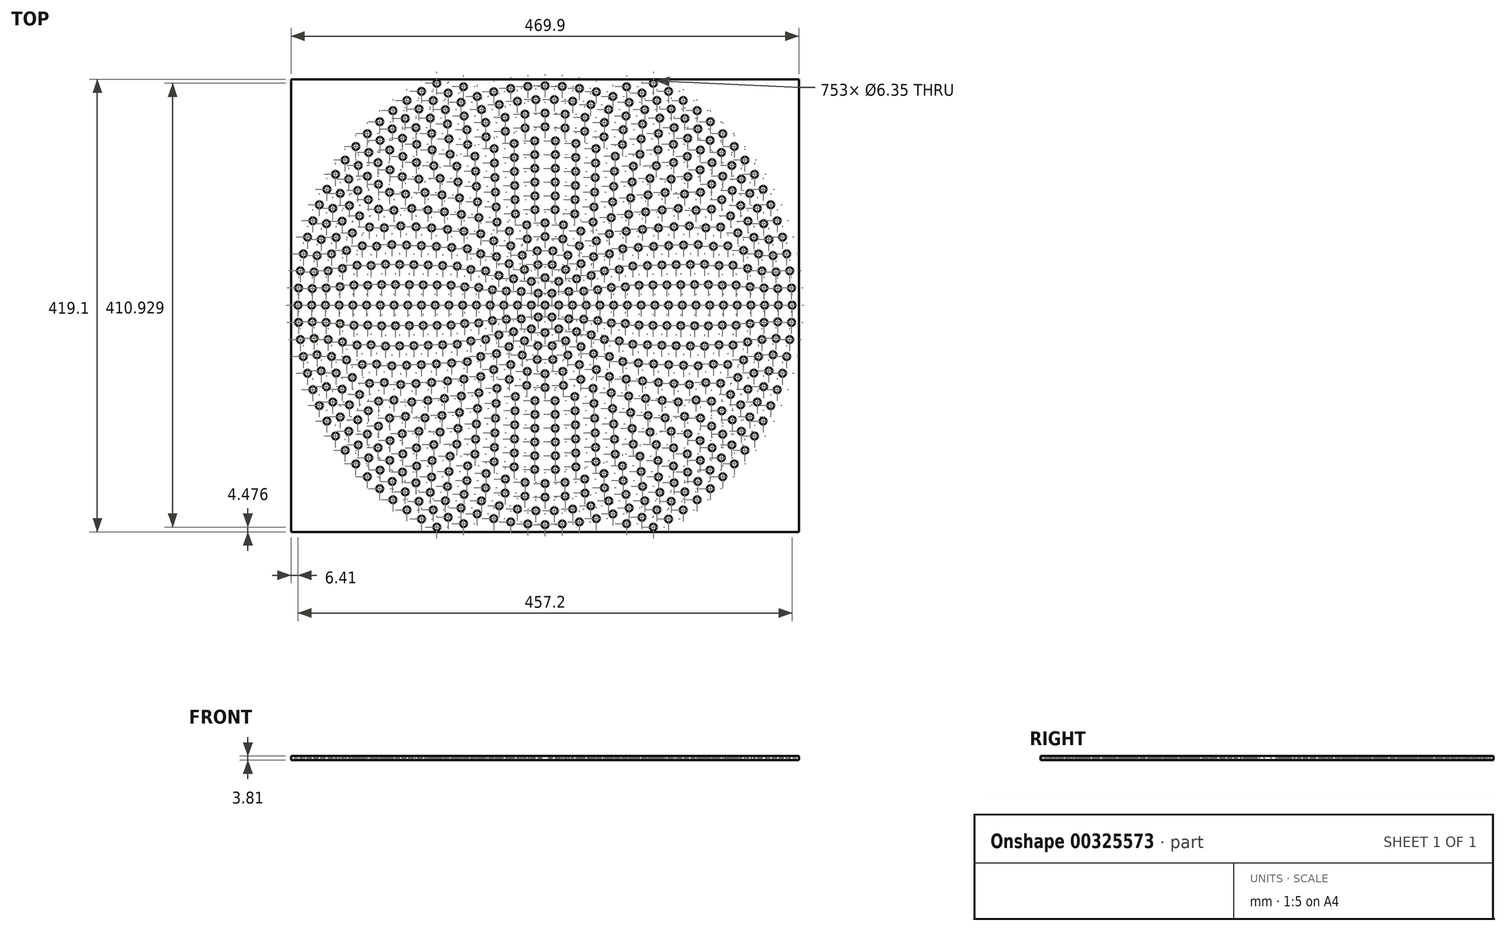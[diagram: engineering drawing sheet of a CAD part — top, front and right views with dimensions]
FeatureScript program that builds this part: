
annotation { "Feature Type Name" : "Feature", "Feature Type Description" : "" }
export const myFeature = defineFeature(function(context is Context, id is Id, definition is map)
    precondition{}
    {
        {
            var Q0;
            Q0=qCreatedBy(makeId("Top.planeOp"),FACE);
            var sketch = newSketch(context, id + "F0", { "sketchPlane" : qUnion([Q0])});
            skLineSegment(sketch, "E0.bottom", {"start": v(-235, 209.16) * mm, "end": v(234.9, 209.16) * mm});
            skLineSegment(sketch, "E0.top", {"start": v(-235, -209.94) * mm, "end": v(234.9, -209.94) * mm});
            skLineSegment(sketch, "E0.left", {"start": v(-235, 209.16) * mm, "end": v(-235, -209.94) * mm});
            skLineSegment(sketch, "E0.right", {"start": v(234.9, 209.16) * mm, "end": v(234.9, -209.94) * mm});
            skPoint(sketch, "E1", {"position": v(-0.06, -209.94) * mm});
            skPoint(sketch, "E2", {"position": v(234.9, -0.39) * mm});
            skCircle(sketch, "E3", {"center": v(0, 0) * mm, "radius": 3.18 * mm});
            skCircle(sketch, "E4.1.0.0", {"center": v(12.7, 0) * mm, "radius": 3.18 * mm});
            skCircle(sketch, "E4.2.0.0", {"center": v(25.4, 0) * mm, "radius": 3.18 * mm});
            skCircle(sketch, "E4.3.0.0", {"center": v(38.1, 0) * mm, "radius": 3.18 * mm});
            skCircle(sketch, "E4.4.0.0", {"center": v(50.8, 0) * mm, "radius": 3.18 * mm});
            skCircle(sketch, "E4.5.0.0", {"center": v(63.5, 0) * mm, "radius": 3.18 * mm});
            skCircle(sketch, "E4.6.0.0", {"center": v(76.2, 0) * mm, "radius": 3.18 * mm});
            skCircle(sketch, "E4.7.0.0", {"center": v(88.9, 0) * mm, "radius": 3.18 * mm});
            skCircle(sketch, "E4.8.0.0", {"center": v(101.6, 0) * mm, "radius": 3.18 * mm});
            skCircle(sketch, "E4.9.0.0", {"center": v(114.3, 0) * mm, "radius": 3.18 * mm});
            skCircle(sketch, "E4.10.0.0", {"center": v(127, 0) * mm, "radius": 3.18 * mm});
            skCircle(sketch, "E4.11.0.0", {"center": v(139.7, 0) * mm, "radius": 3.18 * mm});
            skCircle(sketch, "E4.12.0.0", {"center": v(152.4, 0) * mm, "radius": 3.18 * mm});
            skCircle(sketch, "E4.13.0.0", {"center": v(165.1, 0) * mm, "radius": 3.18 * mm});
            skCircle(sketch, "E4.14.0.0", {"center": v(177.8, 0) * mm, "radius": 3.18 * mm});
            skCircle(sketch, "E4.15.0.0", {"center": v(190.5, 0) * mm, "radius": 3.18 * mm});
            skCircle(sketch, "E4.16.0.0", {"center": v(203.2, 0) * mm, "radius": 3.18 * mm});
            skCircle(sketch, "E4.17.0.0", {"center": v(215.9, 0) * mm, "radius": 3.18 * mm});
            skCircle(sketch, "E4.18.0.0", {"center": v(228.6, 0) * mm, "radius": 3.18 * mm});
            skLineSegment(sketch, "E4.direction1", {"start": v(0, 0) * mm, "end": v(12.7, 0) * mm, "construction": true});
            skCircle(sketch, "E5.1.0", {"center": v(6.35, 11) * mm, "radius": 3.18 * mm});
            skCircle(sketch, "E5.2.0", {"center": v(-6.35, 11) * mm, "radius": 3.18 * mm});
            skCircle(sketch, "E5.3.0", {"center": v(-12.7, 0) * mm, "radius": 3.18 * mm});
            skCircle(sketch, "E5.4.0", {"center": v(-6.35, -11) * mm, "radius": 3.18 * mm});
            skCircle(sketch, "E5.5.0", {"center": v(6.35, -11) * mm, "radius": 3.18 * mm});
            skCircle(sketch, "E6.1.0", {"center": v(22, -12.7) * mm, "radius": 3.18 * mm});
            skCircle(sketch, "E6.2.0", {"center": v(12.7, -22) * mm, "radius": 3.18 * mm});
            skCircle(sketch, "E6.3.0", {"center": v(0, -25.4) * mm, "radius": 3.18 * mm});
            skCircle(sketch, "E6.4.0", {"center": v(-12.7, -22) * mm, "radius": 3.18 * mm});
            skCircle(sketch, "E6.5.0", {"center": v(-22, -12.7) * mm, "radius": 3.18 * mm});
            skCircle(sketch, "E6.6.0", {"center": v(-25.4, 0) * mm, "radius": 3.18 * mm});
            skLineSegment(sketch, "E6.anchor1", {"start": v(0, 0) * mm, "end": v(25.4, 0) * mm, "construction": true});
            skLineSegment(sketch, "E6.anchor2", {"start": v(0, 0) * mm, "end": v(-25.4, 0) * mm, "construction": true});
            skCircle(sketch, "E7.1.0", {"center": v(-22, 12.7) * mm, "radius": 3.18 * mm});
            skCircle(sketch, "E7.2.0", {"center": v(-12.7, 22) * mm, "radius": 3.18 * mm});
            skCircle(sketch, "E7.3.0", {"center": v(0, 25.4) * mm, "radius": 3.18 * mm});
            skCircle(sketch, "E7.4.0", {"center": v(12.7, 22) * mm, "radius": 3.18 * mm});
            skCircle(sketch, "E7.5.0", {"center": v(22, 12.7) * mm, "radius": 3.18 * mm});
            skCircle(sketch, "E8.1.0", {"center": v(35.8, 13.03) * mm, "radius": 3.18 * mm});
            skCircle(sketch, "E8.2.0", {"center": v(29.19, 24.5) * mm, "radius": 3.17 * mm});
            skCircle(sketch, "E8.3.0", {"center": v(19.05, 33) * mm, "radius": 3.18 * mm});
            skCircle(sketch, "E8.4.0", {"center": v(6.62, 37.52) * mm, "radius": 3.17 * mm});
            skCircle(sketch, "E8.5.0", {"center": v(-6.62, 37.52) * mm, "radius": 3.17 * mm});
            skCircle(sketch, "E8.6.0", {"center": v(-19.05, 33) * mm, "radius": 3.17 * mm});
            skCircle(sketch, "E8.7.0", {"center": v(-29.19, 24.5) * mm, "radius": 3.18 * mm});
            skCircle(sketch, "E8.8.0", {"center": v(-35.8, 13.03) * mm, "radius": 3.17 * mm});
            skCircle(sketch, "E8.9.0", {"center": v(-38.1, 0) * mm, "radius": 3.18 * mm});
            skCircle(sketch, "E8.10.0", {"center": v(-35.8, -13.03) * mm, "radius": 3.18 * mm});
            skCircle(sketch, "E9.1.11.0", {"center": v(-29.19, -24.5) * mm, "radius": 3.18 * mm});
            skCircle(sketch, "E10.1.12.0", {"center": v(-19.05, -33) * mm, "radius": 3.18 * mm});
            skCircle(sketch, "E11.1.13.0", {"center": v(-6.62, -37.52) * mm, "radius": 3.18 * mm});
            skCircle(sketch, "E11.1.14.0", {"center": v(6.62, -37.52) * mm, "radius": 3.18 * mm});
            skCircle(sketch, "E12.1.15.0", {"center": v(19.05, -33) * mm, "radius": 3.18 * mm});
            skCircle(sketch, "E13.1.16.0", {"center": v(29.19, -24.5) * mm, "radius": 3.18 * mm});
            skCircle(sketch, "E13.1.17.0", {"center": v(35.8, -13.03) * mm, "radius": 3.18 * mm});
            skCircle(sketch, "E14.1.0", {"center": v(48.74, 14.31) * mm, "radius": 3.17 * mm});
            skCircle(sketch, "E14.2.0", {"center": v(42.74, 27.46) * mm, "radius": 3.18 * mm});
            skCircle(sketch, "E14.3.0", {"center": v(33.27, 38.4) * mm, "radius": 3.18 * mm});
            skCircle(sketch, "E14.4.0", {"center": v(21.1, 46.2) * mm, "radius": 3.17 * mm});
            skCircle(sketch, "E14.5.0", {"center": v(7.23, 50.28) * mm, "radius": 3.18 * mm});
            skCircle(sketch, "E14.6.0", {"center": v(-7.23, 50.28) * mm, "radius": 3.18 * mm});
            skCircle(sketch, "E14.7.0", {"center": v(-21.1, 46.2) * mm, "radius": 3.17 * mm});
            skCircle(sketch, "E14.8.0", {"center": v(-33.27, 38.4) * mm, "radius": 3.17 * mm});
            skCircle(sketch, "E14.9.0", {"center": v(-42.74, 27.46) * mm, "radius": 3.17 * mm});
            skCircle(sketch, "E14.10.0", {"center": v(-48.74, 14.31) * mm, "radius": 3.17 * mm});
            skCircle(sketch, "E14.11.0", {"center": v(-50.8, 0) * mm, "radius": 3.17 * mm});
            skCircle(sketch, "E14.12.0", {"center": v(-48.74, -14.31) * mm, "radius": 3.18 * mm});
            skCircle(sketch, "E14.13.0", {"center": v(-42.74, -27.46) * mm, "radius": 3.18 * mm});
            skCircle(sketch, "E14.14.0", {"center": v(-33.27, -38.4) * mm, "radius": 3.18 * mm});
            skCircle(sketch, "E14.15.0", {"center": v(-21.1, -46.2) * mm, "radius": 3.18 * mm});
            skCircle(sketch, "E14.16.0", {"center": v(-7.23, -50.28) * mm, "radius": 3.18 * mm});
            skCircle(sketch, "E14.17.0", {"center": v(7.23, -50.28) * mm, "radius": 3.18 * mm});
            skCircle(sketch, "E14.18.0", {"center": v(21.1, -46.2) * mm, "radius": 3.18 * mm});
            skCircle(sketch, "E15.1.19.0", {"center": v(33.27, -38.4) * mm, "radius": 3.18 * mm});
            skCircle(sketch, "E16.1.20.0", {"center": v(42.74, -27.46) * mm, "radius": 3.18 * mm});
            skCircle(sketch, "E16.1.21.0", {"center": v(48.74, -14.31) * mm, "radius": 3.18 * mm});
            skCircle(sketch, "E17.1.0", {"center": v(61.34, 16.44) * mm, "radius": 3.18 * mm});
            skCircle(sketch, "E17.2.0", {"center": v(55, 31.75) * mm, "radius": 3.18 * mm});
            skCircle(sketch, "E17.3.0", {"center": v(44.9, 44.9) * mm, "radius": 3.18 * mm});
            skCircle(sketch, "E17.4.0", {"center": v(31.75, 55) * mm, "radius": 3.18 * mm});
            skCircle(sketch, "E17.5.0", {"center": v(16.44, 61.34) * mm, "radius": 3.18 * mm});
            skCircle(sketch, "E17.6.0", {"center": v(0, 63.5) * mm, "radius": 3.18 * mm});
            skCircle(sketch, "E17.7.0", {"center": v(-16.44, 61.34) * mm, "radius": 3.18 * mm});
            skCircle(sketch, "E17.8.0", {"center": v(-31.75, 55) * mm, "radius": 3.18 * mm});
            skCircle(sketch, "E17.9.0", {"center": v(-44.9, 44.9) * mm, "radius": 3.18 * mm});
            skCircle(sketch, "E17.10.0", {"center": v(-55, 31.75) * mm, "radius": 3.18 * mm});
            skCircle(sketch, "E17.11.0", {"center": v(-61.34, 16.44) * mm, "radius": 3.18 * mm});
            skCircle(sketch, "E17.12.0", {"center": v(-63.5, 0) * mm, "radius": 3.18 * mm});
            skCircle(sketch, "E17.13.0", {"center": v(-61.34, -16.44) * mm, "radius": 3.18 * mm});
            skCircle(sketch, "E17.14.0", {"center": v(-55, -31.75) * mm, "radius": 3.18 * mm});
            skCircle(sketch, "E17.15.0", {"center": v(-44.9, -44.9) * mm, "radius": 3.18 * mm});
            skCircle(sketch, "E17.16.0", {"center": v(-31.75, -55) * mm, "radius": 3.18 * mm});
            skCircle(sketch, "E17.17.0", {"center": v(-16.44, -61.34) * mm, "radius": 3.18 * mm});
            skCircle(sketch, "E17.18.0", {"center": v(0, -63.5) * mm, "radius": 3.18 * mm});
            skCircle(sketch, "E17.19.0", {"center": v(16.44, -61.34) * mm, "radius": 3.18 * mm});
            skCircle(sketch, "E17.20.0", {"center": v(31.75, -55) * mm, "radius": 3.18 * mm});
            skCircle(sketch, "E17.21.0", {"center": v(44.9, -44.9) * mm, "radius": 3.18 * mm});
            skCircle(sketch, "E17.22.0", {"center": v(55, -31.75) * mm, "radius": 3.18 * mm});
            skCircle(sketch, "E17.23.0", {"center": v(61.34, -16.44) * mm, "radius": 3.18 * mm});
            skCircle(sketch, "E18.1.0", {"center": v(74.29, 16.96) * mm, "radius": 3.18 * mm});
            skCircle(sketch, "E18.2.0", {"center": v(68.65, 33.06) * mm, "radius": 3.18 * mm});
            skCircle(sketch, "E18.3.0", {"center": v(59.58, 47.5) * mm, "radius": 3.18 * mm});
            skCircle(sketch, "E18.4.0", {"center": v(47.5, 59.58) * mm, "radius": 3.18 * mm});
            skCircle(sketch, "E18.5.0", {"center": v(33.06, 68.65) * mm, "radius": 3.18 * mm});
            skCircle(sketch, "E18.6.0", {"center": v(16.96, 74.29) * mm, "radius": 3.18 * mm});
            skCircle(sketch, "E18.7.0", {"center": v(0, 76.2) * mm, "radius": 3.18 * mm});
            skCircle(sketch, "E18.8.0", {"center": v(-16.96, 74.29) * mm, "radius": 3.18 * mm});
            skCircle(sketch, "E18.9.0", {"center": v(-33.06, 68.65) * mm, "radius": 3.18 * mm});
            skCircle(sketch, "E18.10.0", {"center": v(-47.5, 59.58) * mm, "radius": 3.18 * mm});
            skCircle(sketch, "E18.11.0", {"center": v(-59.58, 47.5) * mm, "radius": 3.17 * mm});
            skCircle(sketch, "E18.12.0", {"center": v(-68.65, 33.06) * mm, "radius": 3.17 * mm});
            skCircle(sketch, "E18.13.0", {"center": v(-74.29, 16.96) * mm, "radius": 3.18 * mm});
            skCircle(sketch, "E18.14.0", {"center": v(-76.2, 0) * mm, "radius": 3.18 * mm});
            skCircle(sketch, "E18.15.0", {"center": v(-74.29, -16.96) * mm, "radius": 3.18 * mm});
            skCircle(sketch, "E18.16.0", {"center": v(-68.65, -33.06) * mm, "radius": 3.17 * mm});
            skCircle(sketch, "E18.17.0", {"center": v(-59.58, -47.5) * mm, "radius": 3.18 * mm});
            skCircle(sketch, "E18.18.0", {"center": v(-47.5, -59.58) * mm, "radius": 3.18 * mm});
            skCircle(sketch, "E18.19.0", {"center": v(-33.06, -68.65) * mm, "radius": 3.18 * mm});
            skCircle(sketch, "E18.20.0", {"center": v(-16.96, -74.29) * mm, "radius": 3.18 * mm});
            skCircle(sketch, "E18.21.0", {"center": v(0, -76.2) * mm, "radius": 3.17 * mm});
            skCircle(sketch, "E18.22.0", {"center": v(16.96, -74.29) * mm, "radius": 3.18 * mm});
            skCircle(sketch, "E18.23.0", {"center": v(33.06, -68.65) * mm, "radius": 3.18 * mm});
            skCircle(sketch, "E18.24.0", {"center": v(47.5, -59.58) * mm, "radius": 3.18 * mm});
            skCircle(sketch, "E18.25.0", {"center": v(59.58, -47.5) * mm, "radius": 3.18 * mm});
            skCircle(sketch, "E19.1.0", {"center": v(86.96, 18.48) * mm, "radius": 3.18 * mm});
            skCircle(sketch, "E19.2.0", {"center": v(81.21, 36.16) * mm, "radius": 3.18 * mm});
            skCircle(sketch, "E19.3.0", {"center": v(71.92, 52.25) * mm, "radius": 3.18 * mm});
            skCircle(sketch, "E19.4.0", {"center": v(59.49, 66.07) * mm, "radius": 3.18 * mm});
            skCircle(sketch, "E19.5.0", {"center": v(44.45, 76.99) * mm, "radius": 3.18 * mm});
            skCircle(sketch, "E19.6.0", {"center": v(27.47, 84.55) * mm, "radius": 3.18 * mm});
            skCircle(sketch, "E19.7.0", {"center": v(9.3, 88.41) * mm, "radius": 3.18 * mm});
            skCircle(sketch, "E19.8.0", {"center": v(-9.3, 88.41) * mm, "radius": 3.18 * mm});
            skCircle(sketch, "E19.9.0", {"center": v(-27.47, 84.55) * mm, "radius": 3.18 * mm});
            skCircle(sketch, "E19.10.0", {"center": v(-44.45, 76.99) * mm, "radius": 3.18 * mm});
            skCircle(sketch, "E19.11.0", {"center": v(-59.49, 66.07) * mm, "radius": 3.17 * mm});
            skCircle(sketch, "E19.12.0", {"center": v(-71.92, 52.25) * mm, "radius": 3.18 * mm});
            skCircle(sketch, "E19.13.0", {"center": v(-81.21, 36.16) * mm, "radius": 3.18 * mm});
            skCircle(sketch, "E19.14.0", {"center": v(-86.96, 18.48) * mm, "radius": 3.18 * mm});
            skCircle(sketch, "E19.15.0", {"center": v(-88.9, 0) * mm, "radius": 3.18 * mm});
            skCircle(sketch, "E19.16.0", {"center": v(-86.96, -18.48) * mm, "radius": 3.17 * mm});
            skCircle(sketch, "E19.17.0", {"center": v(-81.21, -36.16) * mm, "radius": 3.17 * mm});
            skCircle(sketch, "E19.18.0", {"center": v(-71.92, -52.25) * mm, "radius": 3.18 * mm});
            skCircle(sketch, "E19.19.0", {"center": v(-59.49, -66.07) * mm, "radius": 3.18 * mm});
            skCircle(sketch, "E19.20.0", {"center": v(-44.45, -76.99) * mm, "radius": 3.18 * mm});
            skCircle(sketch, "E19.21.0", {"center": v(-27.47, -84.55) * mm, "radius": 3.18 * mm});
            skCircle(sketch, "E19.22.0", {"center": v(-9.3, -88.41) * mm, "radius": 3.18 * mm});
            skCircle(sketch, "E19.23.0", {"center": v(9.3, -88.41) * mm, "radius": 3.18 * mm});
            skCircle(sketch, "E19.24.0", {"center": v(27.47, -84.55) * mm, "radius": 3.18 * mm});
            skCircle(sketch, "E19.25.0", {"center": v(44.45, -76.99) * mm, "radius": 3.18 * mm});
            skCircle(sketch, "E19.26.0", {"center": v(59.49, -66.07) * mm, "radius": 3.18 * mm});
            skCircle(sketch, "E19.27.0", {"center": v(71.92, -52.25) * mm, "radius": 3.18 * mm});
            skCircle(sketch, "E20.1.0", {"center": v(99.87, 18.67) * mm, "radius": 3.18 * mm});
            skCircle(sketch, "E20.2.0", {"center": v(94.74, 36.7) * mm, "radius": 3.18 * mm});
            skCircle(sketch, "E20.3.0", {"center": v(86.38, 53.49) * mm, "radius": 3.18 * mm});
            skCircle(sketch, "E20.4.0", {"center": v(75.08, 68.45) * mm, "radius": 3.17 * mm});
            skCircle(sketch, "E20.5.0", {"center": v(61.23, 81.08) * mm, "radius": 3.18 * mm});
            skCircle(sketch, "E20.6.0", {"center": v(45.29, 90.95) * mm, "radius": 3.18 * mm});
            skCircle(sketch, "E20.7.0", {"center": v(27.8, 97.72) * mm, "radius": 3.18 * mm});
            skCircle(sketch, "E20.8.0", {"center": v(9.37, 101.17) * mm, "radius": 3.17 * mm});
            skCircle(sketch, "E20.9.0", {"center": v(-9.37, 101.17) * mm, "radius": 3.18 * mm});
            skCircle(sketch, "E20.10.0", {"center": v(-27.8, 97.72) * mm, "radius": 3.17 * mm});
            skCircle(sketch, "E20.11.0", {"center": v(-45.29, 90.95) * mm, "radius": 3.17 * mm});
            skCircle(sketch, "E20.12.0", {"center": v(-61.23, 81.08) * mm, "radius": 3.17 * mm});
            skCircle(sketch, "E20.13.0", {"center": v(-75.08, 68.45) * mm, "radius": 3.18 * mm});
            skCircle(sketch, "E20.14.0", {"center": v(-86.38, 53.49) * mm, "radius": 3.18 * mm});
            skCircle(sketch, "E20.15.0", {"center": v(-94.74, 36.7) * mm, "radius": 3.18 * mm});
            skCircle(sketch, "E20.16.0", {"center": v(-99.87, 18.67) * mm, "radius": 3.18 * mm});
            skCircle(sketch, "E20.17.0", {"center": v(-101.6, 0) * mm, "radius": 3.17 * mm});
            skCircle(sketch, "E20.18.0", {"center": v(-99.87, -18.67) * mm, "radius": 3.18 * mm});
            skCircle(sketch, "E20.19.0", {"center": v(-94.74, -36.7) * mm, "radius": 3.18 * mm});
            skCircle(sketch, "E20.20.0", {"center": v(-86.38, -53.49) * mm, "radius": 3.18 * mm});
            skCircle(sketch, "E20.21.0", {"center": v(-75.08, -68.45) * mm, "radius": 3.17 * mm});
            skCircle(sketch, "E20.22.0", {"center": v(-61.23, -81.08) * mm, "radius": 3.18 * mm});
            skCircle(sketch, "E20.23.0", {"center": v(-45.29, -90.95) * mm, "radius": 3.17 * mm});
            skCircle(sketch, "E20.24.0", {"center": v(-27.8, -97.72) * mm, "radius": 3.18 * mm});
            skCircle(sketch, "E20.25.0", {"center": v(-9.37, -101.17) * mm, "radius": 3.18 * mm});
            skCircle(sketch, "E20.26.0", {"center": v(9.37, -101.17) * mm, "radius": 3.17 * mm});
            skCircle(sketch, "E20.27.0", {"center": v(27.8, -97.72) * mm, "radius": 3.17 * mm});
            skCircle(sketch, "E20.28.0", {"center": v(45.29, -90.95) * mm, "radius": 3.17 * mm});
            skCircle(sketch, "E20.29.0", {"center": v(61.23, -81.08) * mm, "radius": 3.17 * mm});
            skCircle(sketch, "E21.1.30.0", {"center": v(75.08, -68.45) * mm, "radius": 3.18 * mm});
            skCircle(sketch, "E21.1.31.0", {"center": v(86.38, -53.49) * mm, "radius": 3.17 * mm});
            skCircle(sketch, "E22.1.32.0", {"center": v(94.74, -36.7) * mm, "radius": 3.18 * mm});
            skCircle(sketch, "E22.1.33.0", {"center": v(99.87, -18.67) * mm, "radius": 3.18 * mm});
            skCircle(sketch, "E23.1.28.0", {"center": v(81.21, -36.16) * mm, "radius": 3.18 * mm});
            skCircle(sketch, "E23.1.29.0", {"center": v(86.96, -18.48) * mm, "radius": 3.18 * mm});
            skCircle(sketch, "E24.1.26.0", {"center": v(68.65, -33.06) * mm, "radius": 3.18 * mm});
            skCircle(sketch, "E24.1.27.0", {"center": v(74.29, -16.96) * mm, "radius": 3.18 * mm});
            skCircle(sketch, "E25.1.0", {"center": v(112.74, 18.81) * mm, "radius": 3.18 * mm});
            skCircle(sketch, "E25.2.0", {"center": v(108.1, 37.11) * mm, "radius": 3.18 * mm});
            skCircle(sketch, "E25.3.0", {"center": v(100.52, 54.4) * mm, "radius": 3.18 * mm});
            skCircle(sketch, "E25.4.0", {"center": v(90.2, 70.2) * mm, "radius": 3.18 * mm});
            skCircle(sketch, "E25.5.0", {"center": v(77.41, 84.1) * mm, "radius": 3.18 * mm});
            skCircle(sketch, "E25.6.0", {"center": v(62.52, 95.69) * mm, "radius": 3.18 * mm});
            skCircle(sketch, "E25.7.0", {"center": v(45.91, 104.67) * mm, "radius": 3.18 * mm});
            skCircle(sketch, "E25.8.0", {"center": v(28.06, 110.8) * mm, "radius": 3.18 * mm});
            skCircle(sketch, "E25.9.0", {"center": v(9.44, 113.9) * mm, "radius": 3.18 * mm});
            skCircle(sketch, "E25.10.0", {"center": v(-9.44, 113.9) * mm, "radius": 3.18 * mm});
            skCircle(sketch, "E25.11.0", {"center": v(-28.06, 110.8) * mm, "radius": 3.18 * mm});
            skCircle(sketch, "E25.12.0", {"center": v(-45.91, 104.67) * mm, "radius": 3.18 * mm});
            skCircle(sketch, "E25.13.0", {"center": v(-62.52, 95.69) * mm, "radius": 3.18 * mm});
            skCircle(sketch, "E25.14.0", {"center": v(-77.41, 84.1) * mm, "radius": 3.18 * mm});
            skCircle(sketch, "E25.15.0", {"center": v(-90.2, 70.2) * mm, "radius": 3.18 * mm});
            skCircle(sketch, "E25.16.0", {"center": v(-100.52, 54.4) * mm, "radius": 3.18 * mm});
            skCircle(sketch, "E25.17.0", {"center": v(-108.1, 37.11) * mm, "radius": 3.18 * mm});
            skCircle(sketch, "E25.18.0", {"center": v(-112.74, 18.81) * mm, "radius": 3.18 * mm});
            skCircle(sketch, "E25.19.0", {"center": v(-114.3, 0) * mm, "radius": 3.18 * mm});
            skCircle(sketch, "E25.20.0", {"center": v(-112.74, -18.81) * mm, "radius": 3.18 * mm});
            skCircle(sketch, "E25.21.0", {"center": v(-108.1, -37.11) * mm, "radius": 3.18 * mm});
            skCircle(sketch, "E25.22.0", {"center": v(-100.52, -54.4) * mm, "radius": 3.18 * mm});
            skCircle(sketch, "E25.23.0", {"center": v(-90.2, -70.2) * mm, "radius": 3.18 * mm});
            skCircle(sketch, "E25.24.0", {"center": v(-77.41, -84.1) * mm, "radius": 3.18 * mm});
            skCircle(sketch, "E25.25.0", {"center": v(-62.52, -95.69) * mm, "radius": 3.18 * mm});
            skCircle(sketch, "E25.26.0", {"center": v(-45.91, -104.67) * mm, "radius": 3.18 * mm});
            skCircle(sketch, "E25.27.0", {"center": v(-28.06, -110.8) * mm, "radius": 3.18 * mm});
            skCircle(sketch, "E25.28.0", {"center": v(-9.44, -113.9) * mm, "radius": 3.18 * mm});
            skCircle(sketch, "E25.29.0", {"center": v(9.44, -113.9) * mm, "radius": 3.18 * mm});
            skCircle(sketch, "E25.30.0", {"center": v(28.06, -110.8) * mm, "radius": 3.18 * mm});
            skCircle(sketch, "E25.31.0", {"center": v(45.91, -104.67) * mm, "radius": 3.18 * mm});
            skCircle(sketch, "E25.32.0", {"center": v(62.52, -95.69) * mm, "radius": 3.18 * mm});
            skCircle(sketch, "E25.33.0", {"center": v(77.41, -84.1) * mm, "radius": 3.18 * mm});
            skCircle(sketch, "E25.34.0", {"center": v(90.2, -70.2) * mm, "radius": 3.18 * mm});
            skCircle(sketch, "E25.35.0", {"center": v(100.52, -54.4) * mm, "radius": 3.18 * mm});
            skCircle(sketch, "E25.36.0", {"center": v(108.1, -37.11) * mm, "radius": 3.18 * mm});
            skCircle(sketch, "E25.37.0", {"center": v(112.74, -18.81) * mm, "radius": 3.18 * mm});
            skCircle(sketch, "E26.1.0", {"center": v(125.58, 18.93) * mm, "radius": 3.18 * mm});
            skCircle(sketch, "E26.2.0", {"center": v(121.36, 37.43) * mm, "radius": 3.18 * mm});
            skCircle(sketch, "E26.3.0", {"center": v(114.42, 55.1) * mm, "radius": 3.18 * mm});
            skCircle(sketch, "E26.4.0", {"center": v(104.93, 71.54) * mm, "radius": 3.18 * mm});
            skCircle(sketch, "E26.5.0", {"center": v(93.1, 86.38) * mm, "radius": 3.18 * mm});
            skCircle(sketch, "E26.6.0", {"center": v(79.18, 99.3) * mm, "radius": 3.18 * mm});
            skCircle(sketch, "E26.7.0", {"center": v(63.5, 109.99) * mm, "radius": 3.18 * mm});
            skCircle(sketch, "E26.8.0", {"center": v(46.4, 118.22) * mm, "radius": 3.18 * mm});
            skCircle(sketch, "E26.9.0", {"center": v(28.26, 123.82) * mm, "radius": 3.18 * mm});
            skCircle(sketch, "E26.10.0", {"center": v(9.5, 126.64) * mm, "radius": 3.18 * mm});
            skCircle(sketch, "E26.11.0", {"center": v(-9.5, 126.64) * mm, "radius": 3.18 * mm});
            skCircle(sketch, "E26.12.0", {"center": v(-28.26, 123.82) * mm, "radius": 3.18 * mm});
            skCircle(sketch, "E26.13.0", {"center": v(-46.4, 118.22) * mm, "radius": 3.18 * mm});
            skCircle(sketch, "E26.14.0", {"center": v(-63.5, 109.99) * mm, "radius": 3.18 * mm});
            skCircle(sketch, "E26.15.0", {"center": v(-79.18, 99.3) * mm, "radius": 3.18 * mm});
            skCircle(sketch, "E26.16.0", {"center": v(-93.1, 86.38) * mm, "radius": 3.18 * mm});
            skCircle(sketch, "E26.17.0", {"center": v(-104.93, 71.54) * mm, "radius": 3.18 * mm});
            skCircle(sketch, "E26.18.0", {"center": v(-114.42, 55.1) * mm, "radius": 3.18 * mm});
            skCircle(sketch, "E26.19.0", {"center": v(-121.36, 37.43) * mm, "radius": 3.18 * mm});
            skCircle(sketch, "E26.20.0", {"center": v(-125.58, 18.93) * mm, "radius": 3.18 * mm});
            skCircle(sketch, "E26.21.0", {"center": v(-127, 0) * mm, "radius": 3.18 * mm});
            skCircle(sketch, "E26.22.0", {"center": v(-125.58, -18.93) * mm, "radius": 3.18 * mm});
            skCircle(sketch, "E26.23.0", {"center": v(-121.36, -37.43) * mm, "radius": 3.18 * mm});
            skCircle(sketch, "E26.24.0", {"center": v(-114.42, -55.1) * mm, "radius": 3.18 * mm});
            skCircle(sketch, "E26.25.0", {"center": v(-104.93, -71.54) * mm, "radius": 3.18 * mm});
            skCircle(sketch, "E26.26.0", {"center": v(-93.1, -86.38) * mm, "radius": 3.18 * mm});
            skCircle(sketch, "E26.27.0", {"center": v(-79.18, -99.3) * mm, "radius": 3.18 * mm});
            skCircle(sketch, "E26.28.0", {"center": v(-63.5, -109.99) * mm, "radius": 3.18 * mm});
            skCircle(sketch, "E26.29.0", {"center": v(-46.4, -118.22) * mm, "radius": 3.18 * mm});
            skCircle(sketch, "E26.30.0", {"center": v(-28.26, -123.82) * mm, "radius": 3.18 * mm});
            skCircle(sketch, "E26.31.0", {"center": v(-9.5, -126.64) * mm, "radius": 3.18 * mm});
            skCircle(sketch, "E26.32.0", {"center": v(9.5, -126.64) * mm, "radius": 3.18 * mm});
            skCircle(sketch, "E26.33.0", {"center": v(28.26, -123.82) * mm, "radius": 3.18 * mm});
            skCircle(sketch, "E26.34.0", {"center": v(46.4, -118.22) * mm, "radius": 3.18 * mm});
            skCircle(sketch, "E26.35.0", {"center": v(63.5, -109.99) * mm, "radius": 3.18 * mm});
            skCircle(sketch, "E26.36.0", {"center": v(79.18, -99.3) * mm, "radius": 3.18 * mm});
            skCircle(sketch, "E26.37.0", {"center": v(93.1, -86.38) * mm, "radius": 3.18 * mm});
            skCircle(sketch, "E26.38.0", {"center": v(104.93, -71.54) * mm, "radius": 3.18 * mm});
            skCircle(sketch, "E26.39.0", {"center": v(114.42, -55.1) * mm, "radius": 3.18 * mm});
            skCircle(sketch, "E26.40.0", {"center": v(121.36, -37.43) * mm, "radius": 3.18 * mm});
            skCircle(sketch, "E26.41.0", {"center": v(125.58, -18.93) * mm, "radius": 3.18 * mm});
            skCircle(sketch, "E27.1.0", {"center": v(138.4, 19.02) * mm, "radius": 3.18 * mm});
            skCircle(sketch, "E27.2.0", {"center": v(134.52, 37.7) * mm, "radius": 3.18 * mm});
            skCircle(sketch, "E27.3.0", {"center": v(128.13, 55.66) * mm, "radius": 3.18 * mm});
            skCircle(sketch, "E27.4.0", {"center": v(119.36, 72.59) * mm, "radius": 3.18 * mm});
            skCircle(sketch, "E27.5.0", {"center": v(108.37, 88.16) * mm, "radius": 3.18 * mm});
            skCircle(sketch, "E27.6.0", {"center": v(95.35, 102.1) * mm, "radius": 3.18 * mm});
            skCircle(sketch, "E27.7.0", {"center": v(80.56, 114.13) * mm, "radius": 3.18 * mm});
            skCircle(sketch, "E27.8.0", {"center": v(64.27, 124.04) * mm, "radius": 3.18 * mm});
            skCircle(sketch, "E27.9.0", {"center": v(46.78, 131.63) * mm, "radius": 3.18 * mm});
            skCircle(sketch, "E27.10.0", {"center": v(28.42, 136.78) * mm, "radius": 3.18 * mm});
            skCircle(sketch, "E27.11.0", {"center": v(9.53, 139.37) * mm, "radius": 3.18 * mm});
            skCircle(sketch, "E27.12.0", {"center": v(-9.53, 139.37) * mm, "radius": 3.18 * mm});
            skCircle(sketch, "E27.13.0", {"center": v(-28.42, 136.78) * mm, "radius": 3.18 * mm});
            skCircle(sketch, "E27.14.0", {"center": v(-46.78, 131.63) * mm, "radius": 3.18 * mm});
            skCircle(sketch, "E27.15.0", {"center": v(-64.27, 124.04) * mm, "radius": 3.18 * mm});
            skCircle(sketch, "E27.16.0", {"center": v(-80.56, 114.13) * mm, "radius": 3.18 * mm});
            skCircle(sketch, "E27.17.0", {"center": v(-95.35, 102.1) * mm, "radius": 3.18 * mm});
            skCircle(sketch, "E27.18.0", {"center": v(-108.37, 88.16) * mm, "radius": 3.18 * mm});
            skCircle(sketch, "E27.19.0", {"center": v(-119.36, 72.59) * mm, "radius": 3.18 * mm});
            skCircle(sketch, "E27.20.0", {"center": v(-128.13, 55.66) * mm, "radius": 3.18 * mm});
            skCircle(sketch, "E27.21.0", {"center": v(-134.52, 37.7) * mm, "radius": 3.18 * mm});
            skCircle(sketch, "E27.22.0", {"center": v(-138.4, 19.02) * mm, "radius": 3.18 * mm});
            skCircle(sketch, "E27.23.0", {"center": v(-139.7, 0) * mm, "radius": 3.18 * mm});
            skCircle(sketch, "E27.24.0", {"center": v(-138.4, -19.02) * mm, "radius": 3.18 * mm});
            skCircle(sketch, "E27.25.0", {"center": v(-134.52, -37.7) * mm, "radius": 3.18 * mm});
            skCircle(sketch, "E27.26.0", {"center": v(-128.13, -55.66) * mm, "radius": 3.18 * mm});
            skCircle(sketch, "E27.27.0", {"center": v(-119.36, -72.59) * mm, "radius": 3.18 * mm});
            skCircle(sketch, "E27.28.0", {"center": v(-108.37, -88.16) * mm, "radius": 3.18 * mm});
            skCircle(sketch, "E27.29.0", {"center": v(-95.35, -102.1) * mm, "radius": 3.18 * mm});
            skCircle(sketch, "E27.30.0", {"center": v(-80.56, -114.13) * mm, "radius": 3.18 * mm});
            skCircle(sketch, "E27.31.0", {"center": v(-64.27, -124.04) * mm, "radius": 3.18 * mm});
            skCircle(sketch, "E27.32.0", {"center": v(-46.78, -131.63) * mm, "radius": 3.18 * mm});
            skCircle(sketch, "E27.33.0", {"center": v(-28.42, -136.78) * mm, "radius": 3.18 * mm});
            skCircle(sketch, "E27.34.0", {"center": v(-9.53, -139.37) * mm, "radius": 3.18 * mm});
            skCircle(sketch, "E27.35.0", {"center": v(9.53, -139.37) * mm, "radius": 3.18 * mm});
            skCircle(sketch, "E27.36.0", {"center": v(28.42, -136.78) * mm, "radius": 3.18 * mm});
            skCircle(sketch, "E27.37.0", {"center": v(46.78, -131.63) * mm, "radius": 3.18 * mm});
            skCircle(sketch, "E27.38.0", {"center": v(64.27, -124.04) * mm, "radius": 3.18 * mm});
            skCircle(sketch, "E27.39.0", {"center": v(80.56, -114.13) * mm, "radius": 3.18 * mm});
            skCircle(sketch, "E27.40.0", {"center": v(95.35, -102.1) * mm, "radius": 3.18 * mm});
            skCircle(sketch, "E27.41.0", {"center": v(108.37, -88.16) * mm, "radius": 3.18 * mm});
            skCircle(sketch, "E27.42.0", {"center": v(119.36, -72.59) * mm, "radius": 3.18 * mm});
            skCircle(sketch, "E27.43.0", {"center": v(128.13, -55.66) * mm, "radius": 3.18 * mm});
            skCircle(sketch, "E27.44.0", {"center": v(134.52, -37.7) * mm, "radius": 3.18 * mm});
            skCircle(sketch, "E27.45.0", {"center": v(138.4, -19.02) * mm, "radius": 3.18 * mm});
            skCircle(sketch, "E28.1.0", {"center": v(151.2, 19.1) * mm, "radius": 3.18 * mm});
            skCircle(sketch, "E28.2.0", {"center": v(147.61, 37.9) * mm, "radius": 3.18 * mm});
            skCircle(sketch, "E28.3.0", {"center": v(141.7, 56.1) * mm, "radius": 3.18 * mm});
            skCircle(sketch, "E28.4.0", {"center": v(133.55, 73.42) * mm, "radius": 3.18 * mm});
            skCircle(sketch, "E28.5.0", {"center": v(123.3, 89.58) * mm, "radius": 3.18 * mm});
            skCircle(sketch, "E28.6.0", {"center": v(111.1, 104.32) * mm, "radius": 3.18 * mm});
            skCircle(sketch, "E28.7.0", {"center": v(97.14, 117.43) * mm, "radius": 3.18 * mm});
            skCircle(sketch, "E28.8.0", {"center": v(81.66, 128.68) * mm, "radius": 3.18 * mm});
            skCircle(sketch, "E28.9.0", {"center": v(64.89, 137.9) * mm, "radius": 3.18 * mm});
            skCircle(sketch, "E28.10.0", {"center": v(47.1, 144.94) * mm, "radius": 3.18 * mm});
            skCircle(sketch, "E28.11.0", {"center": v(28.56, 149.7) * mm, "radius": 3.18 * mm});
            skCircle(sketch, "E28.12.0", {"center": v(9.57, 152.1) * mm, "radius": 3.18 * mm});
            skCircle(sketch, "E28.13.0", {"center": v(-9.57, 152.1) * mm, "radius": 3.18 * mm});
            skCircle(sketch, "E28.14.0", {"center": v(-28.56, 149.7) * mm, "radius": 3.18 * mm});
            skCircle(sketch, "E28.15.0", {"center": v(-47.1, 144.94) * mm, "radius": 3.17 * mm});
            skCircle(sketch, "E28.16.0", {"center": v(-64.89, 137.9) * mm, "radius": 3.18 * mm});
            skCircle(sketch, "E28.17.0", {"center": v(-81.66, 128.68) * mm, "radius": 3.18 * mm});
            skCircle(sketch, "E28.18.0", {"center": v(-97.14, 117.43) * mm, "radius": 3.18 * mm});
            skCircle(sketch, "E28.19.0", {"center": v(-111.1, 104.32) * mm, "radius": 3.18 * mm});
            skCircle(sketch, "E28.20.0", {"center": v(-123.3, 89.58) * mm, "radius": 3.18 * mm});
            skCircle(sketch, "E28.21.0", {"center": v(-133.55, 73.42) * mm, "radius": 3.17 * mm});
            skCircle(sketch, "E28.22.0", {"center": v(-141.7, 56.1) * mm, "radius": 3.18 * mm});
            skCircle(sketch, "E28.23.0", {"center": v(-147.61, 37.9) * mm, "radius": 3.18 * mm});
            skCircle(sketch, "E28.24.0", {"center": v(-151.2, 19.1) * mm, "radius": 3.18 * mm});
            skCircle(sketch, "E28.25.0", {"center": v(-152.4, 0) * mm, "radius": 3.18 * mm});
            skCircle(sketch, "E28.26.0", {"center": v(-151.2, -19.1) * mm, "radius": 3.18 * mm});
            skCircle(sketch, "E28.27.0", {"center": v(-147.61, -37.9) * mm, "radius": 3.18 * mm});
            skCircle(sketch, "E28.28.0", {"center": v(-141.7, -56.1) * mm, "radius": 3.18 * mm});
            skCircle(sketch, "E28.29.0", {"center": v(-133.55, -73.42) * mm, "radius": 3.18 * mm});
            skCircle(sketch, "E28.30.0", {"center": v(-123.3, -89.58) * mm, "radius": 3.18 * mm});
            skCircle(sketch, "E28.31.0", {"center": v(-111.1, -104.32) * mm, "radius": 3.18 * mm});
            skCircle(sketch, "E28.32.0", {"center": v(-97.14, -117.43) * mm, "radius": 3.18 * mm});
            skCircle(sketch, "E28.33.0", {"center": v(-81.66, -128.68) * mm, "radius": 3.18 * mm});
            skCircle(sketch, "E28.34.0", {"center": v(-64.89, -137.9) * mm, "radius": 3.18 * mm});
            skCircle(sketch, "E28.35.0", {"center": v(-47.1, -144.94) * mm, "radius": 3.18 * mm});
            skCircle(sketch, "E28.36.0", {"center": v(-28.56, -149.7) * mm, "radius": 3.18 * mm});
            skCircle(sketch, "E28.37.0", {"center": v(-9.57, -152.1) * mm, "radius": 3.18 * mm});
            skCircle(sketch, "E28.38.0", {"center": v(9.57, -152.1) * mm, "radius": 3.18 * mm});
            skCircle(sketch, "E28.39.0", {"center": v(28.56, -149.7) * mm, "radius": 3.18 * mm});
            skCircle(sketch, "E28.40.0", {"center": v(47.1, -144.94) * mm, "radius": 3.18 * mm});
            skCircle(sketch, "E28.41.0", {"center": v(64.89, -137.9) * mm, "radius": 3.18 * mm});
            skCircle(sketch, "E28.42.0", {"center": v(81.66, -128.68) * mm, "radius": 3.18 * mm});
            skCircle(sketch, "E28.43.0", {"center": v(97.14, -117.43) * mm, "radius": 3.18 * mm});
            skCircle(sketch, "E28.44.0", {"center": v(111.1, -104.32) * mm, "radius": 3.18 * mm});
            skCircle(sketch, "E28.45.0", {"center": v(123.3, -89.58) * mm, "radius": 3.18 * mm});
            skCircle(sketch, "E28.46.0", {"center": v(133.55, -73.42) * mm, "radius": 3.18 * mm});
            skCircle(sketch, "E28.47.0", {"center": v(141.7, -56.1) * mm, "radius": 3.18 * mm});
            skCircle(sketch, "E28.48.0", {"center": v(147.61, -37.9) * mm, "radius": 3.18 * mm});
            skCircle(sketch, "E28.49.0", {"center": v(151.2, -19.1) * mm, "radius": 3.18 * mm});
            skCircle(sketch, "E29.1.0", {"center": v(164.06, 18.49) * mm, "radius": 3.18 * mm});
            skCircle(sketch, "E29.2.0", {"center": v(160.96, 36.74) * mm, "radius": 3.18 * mm});
            skCircle(sketch, "E29.3.0", {"center": v(155.84, 54.53) * mm, "radius": 3.18 * mm});
            skCircle(sketch, "E29.4.0", {"center": v(148.75, 71.63) * mm, "radius": 3.18 * mm});
            skCircle(sketch, "E29.5.0", {"center": v(139.8, 87.84) * mm, "radius": 3.18 * mm});
            skCircle(sketch, "E29.6.0", {"center": v(129.08, 102.94) * mm, "radius": 3.18 * mm});
            skCircle(sketch, "E29.7.0", {"center": v(116.74, 116.74) * mm, "radius": 3.18 * mm});
            skCircle(sketch, "E29.8.0", {"center": v(102.94, 129.08) * mm, "radius": 3.18 * mm});
            skCircle(sketch, "E29.9.0", {"center": v(87.84, 139.8) * mm, "radius": 3.18 * mm});
            skCircle(sketch, "E29.10.0", {"center": v(71.63, 148.75) * mm, "radius": 3.18 * mm});
            skCircle(sketch, "E29.11.0", {"center": v(54.53, 155.84) * mm, "radius": 3.18 * mm});
            skCircle(sketch, "E29.12.0", {"center": v(36.74, 160.96) * mm, "radius": 3.18 * mm});
            skCircle(sketch, "E29.13.0", {"center": v(18.49, 164.06) * mm, "radius": 3.18 * mm});
            skCircle(sketch, "E29.14.0", {"center": v(0, 165.1) * mm, "radius": 3.18 * mm});
            skCircle(sketch, "E29.15.0", {"center": v(-18.49, 164.06) * mm, "radius": 3.18 * mm});
            skCircle(sketch, "E29.16.0", {"center": v(-36.74, 160.96) * mm, "radius": 3.18 * mm});
            skCircle(sketch, "E29.17.0", {"center": v(-54.53, 155.84) * mm, "radius": 3.18 * mm});
            skCircle(sketch, "E29.18.0", {"center": v(-71.63, 148.75) * mm, "radius": 3.18 * mm});
            skCircle(sketch, "E29.19.0", {"center": v(-87.84, 139.8) * mm, "radius": 3.18 * mm});
            skCircle(sketch, "E29.20.0", {"center": v(-102.94, 129.08) * mm, "radius": 3.18 * mm});
            skCircle(sketch, "E29.21.0", {"center": v(-116.74, 116.74) * mm, "radius": 3.18 * mm});
            skCircle(sketch, "E29.22.0", {"center": v(-129.08, 102.94) * mm, "radius": 3.18 * mm});
            skCircle(sketch, "E29.23.0", {"center": v(-139.8, 87.84) * mm, "radius": 3.18 * mm});
            skCircle(sketch, "E29.24.0", {"center": v(-148.75, 71.63) * mm, "radius": 3.18 * mm});
            skCircle(sketch, "E29.25.0", {"center": v(-155.84, 54.53) * mm, "radius": 3.18 * mm});
            skCircle(sketch, "E29.26.0", {"center": v(-160.96, 36.74) * mm, "radius": 3.18 * mm});
            skCircle(sketch, "E29.27.0", {"center": v(-164.06, 18.49) * mm, "radius": 3.18 * mm});
            skCircle(sketch, "E29.28.0", {"center": v(-165.1, 0) * mm, "radius": 3.18 * mm});
            skCircle(sketch, "E29.29.0", {"center": v(-164.06, -18.49) * mm, "radius": 3.18 * mm});
            skCircle(sketch, "E29.30.0", {"center": v(-160.96, -36.74) * mm, "radius": 3.18 * mm});
            skCircle(sketch, "E29.31.0", {"center": v(-155.84, -54.53) * mm, "radius": 3.18 * mm});
            skCircle(sketch, "E29.32.0", {"center": v(-148.75, -71.63) * mm, "radius": 3.18 * mm});
            skCircle(sketch, "E29.33.0", {"center": v(-139.8, -87.84) * mm, "radius": 3.18 * mm});
            skCircle(sketch, "E29.34.0", {"center": v(-129.08, -102.94) * mm, "radius": 3.18 * mm});
            skCircle(sketch, "E29.35.0", {"center": v(-116.74, -116.74) * mm, "radius": 3.18 * mm});
            skCircle(sketch, "E29.36.0", {"center": v(-102.94, -129.08) * mm, "radius": 3.18 * mm});
            skCircle(sketch, "E29.37.0", {"center": v(-87.84, -139.8) * mm, "radius": 3.18 * mm});
            skCircle(sketch, "E29.38.0", {"center": v(-71.63, -148.75) * mm, "radius": 3.18 * mm});
            skCircle(sketch, "E29.39.0", {"center": v(-54.53, -155.84) * mm, "radius": 3.18 * mm});
            skCircle(sketch, "E29.40.0", {"center": v(-36.74, -160.96) * mm, "radius": 3.18 * mm});
            skCircle(sketch, "E29.41.0", {"center": v(-18.49, -164.06) * mm, "radius": 3.18 * mm});
            skCircle(sketch, "E29.42.0", {"center": v(0, -165.1) * mm, "radius": 3.18 * mm});
            skCircle(sketch, "E29.43.0", {"center": v(18.49, -164.06) * mm, "radius": 3.18 * mm});
            skCircle(sketch, "E29.44.0", {"center": v(36.74, -160.96) * mm, "radius": 3.18 * mm});
            skCircle(sketch, "E29.45.0", {"center": v(54.53, -155.84) * mm, "radius": 3.18 * mm});
            skCircle(sketch, "E29.46.0", {"center": v(71.63, -148.75) * mm, "radius": 3.18 * mm});
            skCircle(sketch, "E29.47.0", {"center": v(87.84, -139.8) * mm, "radius": 3.17 * mm});
            skCircle(sketch, "E29.48.0", {"center": v(102.94, -129.08) * mm, "radius": 3.18 * mm});
            skCircle(sketch, "E29.49.0", {"center": v(116.74, -116.74) * mm, "radius": 3.18 * mm});
            skCircle(sketch, "E29.50.0", {"center": v(129.08, -102.94) * mm, "radius": 3.18 * mm});
            skCircle(sketch, "E29.51.0", {"center": v(139.8, -87.84) * mm, "radius": 3.18 * mm});
            skCircle(sketch, "E29.52.0", {"center": v(148.75, -71.63) * mm, "radius": 3.18 * mm});
            skCircle(sketch, "E29.53.0", {"center": v(155.84, -54.53) * mm, "radius": 3.18 * mm});
            skCircle(sketch, "E29.54.0", {"center": v(160.96, -36.74) * mm, "radius": 3.18 * mm});
            skCircle(sketch, "E29.55.0", {"center": v(164.06, -18.49) * mm, "radius": 3.18 * mm});
            skCircle(sketch, "E30.1.0", {"center": v(176.83, 18.59) * mm, "radius": 3.18 * mm});
            skCircle(sketch, "E30.2.0", {"center": v(173.91, 36.97) * mm, "radius": 3.18 * mm});
            skCircle(sketch, "E30.3.0", {"center": v(169.1, 54.94) * mm, "radius": 3.18 * mm});
            skCircle(sketch, "E30.4.0", {"center": v(162.43, 72.32) * mm, "radius": 3.18 * mm});
            skCircle(sketch, "E30.5.0", {"center": v(153.98, 88.9) * mm, "radius": 3.18 * mm});
            skCircle(sketch, "E30.6.0", {"center": v(143.84, 104.5) * mm, "radius": 3.18 * mm});
            skCircle(sketch, "E30.7.0", {"center": v(132.13, 118.97) * mm, "radius": 3.18 * mm});
            skCircle(sketch, "E30.8.0", {"center": v(118.97, 132.13) * mm, "radius": 3.17 * mm});
            skCircle(sketch, "E30.9.0", {"center": v(104.5, 143.84) * mm, "radius": 3.18 * mm});
            skCircle(sketch, "E30.10.0", {"center": v(88.9, 153.98) * mm, "radius": 3.18 * mm});
            skCircle(sketch, "E30.11.0", {"center": v(72.32, 162.43) * mm, "radius": 3.18 * mm});
            skCircle(sketch, "E30.12.0", {"center": v(54.94, 169.1) * mm, "radius": 3.18 * mm});
            skCircle(sketch, "E30.13.0", {"center": v(36.97, 173.91) * mm, "radius": 3.18 * mm});
            skCircle(sketch, "E30.14.0", {"center": v(18.59, 176.83) * mm, "radius": 3.18 * mm});
            skCircle(sketch, "E30.15.0", {"center": v(0, 177.8) * mm, "radius": 3.18 * mm});
            skCircle(sketch, "E30.16.0", {"center": v(-18.59, 176.83) * mm, "radius": 3.18 * mm});
            skCircle(sketch, "E30.17.0", {"center": v(-36.97, 173.91) * mm, "radius": 3.18 * mm});
            skCircle(sketch, "E30.18.0", {"center": v(-54.94, 169.1) * mm, "radius": 3.18 * mm});
            skCircle(sketch, "E30.19.0", {"center": v(-72.32, 162.43) * mm, "radius": 3.18 * mm});
            skCircle(sketch, "E30.20.0", {"center": v(-88.9, 153.98) * mm, "radius": 3.18 * mm});
            skCircle(sketch, "E30.21.0", {"center": v(-104.5, 143.84) * mm, "radius": 3.17 * mm});
            skCircle(sketch, "E30.22.0", {"center": v(-118.97, 132.13) * mm, "radius": 3.18 * mm});
            skCircle(sketch, "E30.23.0", {"center": v(-132.13, 118.97) * mm, "radius": 3.18 * mm});
            skCircle(sketch, "E30.24.0", {"center": v(-143.84, 104.5) * mm, "radius": 3.18 * mm});
            skCircle(sketch, "E30.25.0", {"center": v(-153.98, 88.9) * mm, "radius": 3.18 * mm});
            skCircle(sketch, "E30.26.0", {"center": v(-162.43, 72.32) * mm, "radius": 3.18 * mm});
            skCircle(sketch, "E30.27.0", {"center": v(-169.1, 54.94) * mm, "radius": 3.18 * mm});
            skCircle(sketch, "E30.28.0", {"center": v(-173.91, 36.97) * mm, "radius": 3.18 * mm});
            skCircle(sketch, "E30.29.0", {"center": v(-176.83, 18.59) * mm, "radius": 3.18 * mm});
            skCircle(sketch, "E30.30.0", {"center": v(-177.8, 0) * mm, "radius": 3.18 * mm});
            skCircle(sketch, "E30.31.0", {"center": v(-176.83, -18.59) * mm, "radius": 3.18 * mm});
            skCircle(sketch, "E30.32.0", {"center": v(-173.91, -36.97) * mm, "radius": 3.18 * mm});
            skCircle(sketch, "E30.33.0", {"center": v(-169.1, -54.94) * mm, "radius": 3.18 * mm});
            skCircle(sketch, "E30.34.0", {"center": v(-162.43, -72.32) * mm, "radius": 3.17 * mm});
            skCircle(sketch, "E30.35.0", {"center": v(-153.98, -88.9) * mm, "radius": 3.18 * mm});
            skCircle(sketch, "E30.36.0", {"center": v(-143.84, -104.5) * mm, "radius": 3.18 * mm});
            skCircle(sketch, "E30.37.0", {"center": v(-132.13, -118.97) * mm, "radius": 3.18 * mm});
            skCircle(sketch, "E30.38.0", {"center": v(-118.97, -132.13) * mm, "radius": 3.18 * mm});
            skCircle(sketch, "E30.39.0", {"center": v(-104.5, -143.84) * mm, "radius": 3.18 * mm});
            skCircle(sketch, "E30.40.0", {"center": v(-88.9, -153.98) * mm, "radius": 3.18 * mm});
            skCircle(sketch, "E30.41.0", {"center": v(-72.32, -162.43) * mm, "radius": 3.18 * mm});
            skCircle(sketch, "E30.42.0", {"center": v(-54.94, -169.1) * mm, "radius": 3.18 * mm});
            skCircle(sketch, "E30.43.0", {"center": v(-36.97, -173.91) * mm, "radius": 3.18 * mm});
            skCircle(sketch, "E30.44.0", {"center": v(-18.59, -176.83) * mm, "radius": 3.18 * mm});
            skCircle(sketch, "E30.45.0", {"center": v(0, -177.8) * mm, "radius": 3.18 * mm});
            skCircle(sketch, "E30.46.0", {"center": v(18.59, -176.83) * mm, "radius": 3.18 * mm});
            skCircle(sketch, "E30.47.0", {"center": v(36.97, -173.91) * mm, "radius": 3.18 * mm});
            skCircle(sketch, "E30.48.0", {"center": v(54.94, -169.1) * mm, "radius": 3.18 * mm});
            skCircle(sketch, "E30.49.0", {"center": v(72.32, -162.43) * mm, "radius": 3.18 * mm});
            skCircle(sketch, "E30.50.0", {"center": v(88.9, -153.98) * mm, "radius": 3.18 * mm});
            skCircle(sketch, "E30.51.0", {"center": v(104.5, -143.84) * mm, "radius": 3.18 * mm});
            skCircle(sketch, "E30.52.0", {"center": v(118.97, -132.13) * mm, "radius": 3.18 * mm});
            skCircle(sketch, "E30.53.0", {"center": v(132.13, -118.97) * mm, "radius": 3.18 * mm});
            skCircle(sketch, "E30.54.0", {"center": v(143.84, -104.5) * mm, "radius": 3.18 * mm});
            skCircle(sketch, "E30.55.0", {"center": v(153.98, -88.9) * mm, "radius": 3.18 * mm});
            skCircle(sketch, "E30.56.0", {"center": v(162.43, -72.32) * mm, "radius": 3.18 * mm});
            skCircle(sketch, "E30.57.0", {"center": v(169.1, -54.94) * mm, "radius": 3.18 * mm});
            skCircle(sketch, "E30.58.0", {"center": v(173.91, -36.97) * mm, "radius": 3.18 * mm});
            skCircle(sketch, "E30.59.0", {"center": v(176.83, -18.59) * mm, "radius": 3.18 * mm});
            skCircle(sketch, "E31.1.0", {"center": v(189.73, 17.08) * mm, "radius": 3.18 * mm});
            skCircle(sketch, "E31.2.0", {"center": v(187.44, 34.02) * mm, "radius": 3.18 * mm});
            skCircle(sketch, "E31.3.0", {"center": v(183.63, 50.68) * mm, "radius": 3.18 * mm});
            skCircle(sketch, "E31.4.0", {"center": v(178.35, 66.94) * mm, "radius": 3.18 * mm});
            skCircle(sketch, "E31.5.0", {"center": v(171.63, 82.65) * mm, "radius": 3.18 * mm});
            skCircle(sketch, "E31.6.0", {"center": v(163.53, 97.7) * mm, "radius": 3.18 * mm});
            skCircle(sketch, "E31.7.0", {"center": v(154.12, 111.97) * mm, "radius": 3.18 * mm});
            skCircle(sketch, "E31.8.0", {"center": v(143.46, 125.34) * mm, "radius": 3.18 * mm});
            skCircle(sketch, "E31.9.0", {"center": v(131.65, 137.7) * mm, "radius": 3.18 * mm});
            skCircle(sketch, "E31.10.0", {"center": v(118.77, 148.94) * mm, "radius": 3.18 * mm});
            skCircle(sketch, "E31.11.0", {"center": v(104.95, 158.99) * mm, "radius": 3.18 * mm});
            skCircle(sketch, "E31.12.0", {"center": v(90.27, 167.75) * mm, "radius": 3.18 * mm});
            skCircle(sketch, "E31.13.0", {"center": v(74.87, 175.17) * mm, "radius": 3.18 * mm});
            skCircle(sketch, "E31.14.0", {"center": v(58.87, 181.18) * mm, "radius": 3.18 * mm});
            skCircle(sketch, "E31.15.0", {"center": v(42.4, 185.72) * mm, "radius": 3.18 * mm});
            skCircle(sketch, "E31.16.0", {"center": v(25.57, 188.78) * mm, "radius": 3.18 * mm});
            skCircle(sketch, "E31.17.0", {"center": v(8.55, 190.3) * mm, "radius": 3.18 * mm});
            skCircle(sketch, "E31.18.0", {"center": v(-8.55, 190.3) * mm, "radius": 3.18 * mm});
            skCircle(sketch, "E31.19.0", {"center": v(-25.57, 188.78) * mm, "radius": 3.18 * mm});
            skCircle(sketch, "E31.20.0", {"center": v(-42.4, 185.72) * mm, "radius": 3.18 * mm});
            skCircle(sketch, "E31.21.0", {"center": v(-58.87, 181.18) * mm, "radius": 3.18 * mm});
            skCircle(sketch, "E31.22.0", {"center": v(-74.87, 175.17) * mm, "radius": 3.18 * mm});
            skCircle(sketch, "E31.23.0", {"center": v(-90.27, 167.75) * mm, "radius": 3.18 * mm});
            skCircle(sketch, "E31.24.0", {"center": v(-104.95, 158.99) * mm, "radius": 3.18 * mm});
            skCircle(sketch, "E31.25.0", {"center": v(-118.77, 148.94) * mm, "radius": 3.18 * mm});
            skCircle(sketch, "E31.26.0", {"center": v(-131.65, 137.7) * mm, "radius": 3.18 * mm});
            skCircle(sketch, "E31.27.0", {"center": v(-143.46, 125.34) * mm, "radius": 3.18 * mm});
            skCircle(sketch, "E31.28.0", {"center": v(-154.12, 111.97) * mm, "radius": 3.18 * mm});
            skCircle(sketch, "E31.29.0", {"center": v(-163.53, 97.7) * mm, "radius": 3.18 * mm});
            skCircle(sketch, "E31.30.0", {"center": v(-171.63, 82.65) * mm, "radius": 3.18 * mm});
            skCircle(sketch, "E31.31.0", {"center": v(-178.35, 66.94) * mm, "radius": 3.18 * mm});
            skCircle(sketch, "E31.32.0", {"center": v(-183.63, 50.68) * mm, "radius": 3.18 * mm});
            skCircle(sketch, "E31.33.0", {"center": v(-187.44, 34.02) * mm, "radius": 3.18 * mm});
            skCircle(sketch, "E31.34.0", {"center": v(-189.73, 17.08) * mm, "radius": 3.18 * mm});
            skCircle(sketch, "E31.35.0", {"center": v(-190.5, 0) * mm, "radius": 3.18 * mm});
            skCircle(sketch, "E31.36.0", {"center": v(-189.73, -17.08) * mm, "radius": 3.18 * mm});
            skCircle(sketch, "E31.37.0", {"center": v(-187.44, -34.02) * mm, "radius": 3.18 * mm});
            skCircle(sketch, "E31.38.0", {"center": v(-183.63, -50.68) * mm, "radius": 3.18 * mm});
            skCircle(sketch, "E31.39.0", {"center": v(-178.35, -66.94) * mm, "radius": 3.18 * mm});
            skCircle(sketch, "E31.40.0", {"center": v(-171.63, -82.65) * mm, "radius": 3.18 * mm});
            skCircle(sketch, "E31.41.0", {"center": v(-163.53, -97.7) * mm, "radius": 3.18 * mm});
            skCircle(sketch, "E31.42.0", {"center": v(-154.12, -111.97) * mm, "radius": 3.18 * mm});
            skCircle(sketch, "E31.43.0", {"center": v(-143.46, -125.34) * mm, "radius": 3.18 * mm});
            skCircle(sketch, "E31.44.0", {"center": v(-131.65, -137.7) * mm, "radius": 3.18 * mm});
            skCircle(sketch, "E31.45.0", {"center": v(-118.77, -148.94) * mm, "radius": 3.18 * mm});
            skCircle(sketch, "E31.46.0", {"center": v(-104.95, -158.99) * mm, "radius": 3.18 * mm});
            skCircle(sketch, "E31.47.0", {"center": v(-90.27, -167.75) * mm, "radius": 3.18 * mm});
            skCircle(sketch, "E31.48.0", {"center": v(-74.87, -175.17) * mm, "radius": 3.18 * mm});
            skCircle(sketch, "E31.49.0", {"center": v(-58.87, -181.18) * mm, "radius": 3.18 * mm});
            skCircle(sketch, "E31.50.0", {"center": v(-42.4, -185.72) * mm, "radius": 3.18 * mm});
            skCircle(sketch, "E31.51.0", {"center": v(-25.57, -188.78) * mm, "radius": 3.18 * mm});
            skCircle(sketch, "E31.52.0", {"center": v(-8.55, -190.3) * mm, "radius": 3.17 * mm});
            skCircle(sketch, "E31.53.0", {"center": v(8.55, -190.3) * mm, "radius": 3.18 * mm});
            skCircle(sketch, "E31.54.0", {"center": v(25.57, -188.78) * mm, "radius": 3.18 * mm});
            skCircle(sketch, "E31.55.0", {"center": v(42.4, -185.72) * mm, "radius": 3.18 * mm});
            skCircle(sketch, "E31.56.0", {"center": v(58.87, -181.18) * mm, "radius": 3.18 * mm});
            skCircle(sketch, "E31.57.0", {"center": v(74.87, -175.17) * mm, "radius": 3.18 * mm});
            skCircle(sketch, "E31.58.0", {"center": v(90.27, -167.75) * mm, "radius": 3.18 * mm});
            skCircle(sketch, "E31.59.0", {"center": v(104.95, -158.99) * mm, "radius": 3.18 * mm});
            skCircle(sketch, "E31.60.0", {"center": v(118.77, -148.94) * mm, "radius": 3.18 * mm});
            skCircle(sketch, "E31.61.0", {"center": v(131.65, -137.7) * mm, "radius": 3.18 * mm});
            skCircle(sketch, "E31.62.0", {"center": v(143.46, -125.34) * mm, "radius": 3.18 * mm});
            skCircle(sketch, "E31.63.0", {"center": v(154.12, -111.97) * mm, "radius": 3.18 * mm});
            skCircle(sketch, "E31.64.0", {"center": v(163.53, -97.7) * mm, "radius": 3.18 * mm});
            skCircle(sketch, "E31.65.0", {"center": v(171.63, -82.65) * mm, "radius": 3.18 * mm});
            skCircle(sketch, "E31.66.0", {"center": v(178.35, -66.94) * mm, "radius": 3.18 * mm});
            skCircle(sketch, "E31.67.0", {"center": v(183.63, -50.68) * mm, "radius": 3.18 * mm});
            skCircle(sketch, "E31.68.0", {"center": v(187.44, -34.02) * mm, "radius": 3.18 * mm});
            skCircle(sketch, "E31.69.0", {"center": v(189.73, -17.08) * mm, "radius": 3.18 * mm});
            skCircle(sketch, "E32.1.0", {"center": v(202.57, 15.94) * mm, "radius": 3.18 * mm});
            skCircle(sketch, "E32.2.0", {"center": v(200.7, 31.79) * mm, "radius": 3.18 * mm});
            skCircle(sketch, "E32.3.0", {"center": v(197.59, 47.44) * mm, "radius": 3.18 * mm});
            skCircle(sketch, "E32.4.0", {"center": v(193.25, 62.8) * mm, "radius": 3.18 * mm});
            skCircle(sketch, "E32.5.0", {"center": v(187.73, 77.76) * mm, "radius": 3.18 * mm});
            skCircle(sketch, "E32.6.0", {"center": v(181.05, 92.25) * mm, "radius": 3.18 * mm});
            skCircle(sketch, "E32.7.0", {"center": v(173.26, 106.17) * mm, "radius": 3.18 * mm});
            skCircle(sketch, "E32.8.0", {"center": v(164.4, 119.44) * mm, "radius": 3.18 * mm});
            skCircle(sketch, "E32.9.0", {"center": v(154.51, 131.97) * mm, "radius": 3.18 * mm});
            skCircle(sketch, "E32.10.0", {"center": v(143.68, 143.68) * mm, "radius": 3.18 * mm});
            skCircle(sketch, "E32.11.0", {"center": v(131.97, 154.51) * mm, "radius": 3.18 * mm});
            skCircle(sketch, "E32.12.0", {"center": v(119.44, 164.4) * mm, "radius": 3.18 * mm});
            skCircle(sketch, "E32.13.0", {"center": v(106.17, 173.26) * mm, "radius": 3.18 * mm});
            skCircle(sketch, "E32.14.0", {"center": v(92.25, 181.05) * mm, "radius": 3.18 * mm});
            skCircle(sketch, "E32.15.0", {"center": v(77.76, 187.73) * mm, "radius": 3.18 * mm});
            skCircle(sketch, "E32.16.0", {"center": v(62.8, 193.25) * mm, "radius": 3.18 * mm});
            skCircle(sketch, "E32.17.0", {"center": v(47.44, 197.59) * mm, "radius": 3.18 * mm});
            skCircle(sketch, "E32.18.0", {"center": v(31.79, 200.7) * mm, "radius": 3.18 * mm});
            skCircle(sketch, "E32.19.0", {"center": v(15.94, 202.57) * mm, "radius": 3.18 * mm});
            skCircle(sketch, "E32.20.0", {"center": v(0, 203.2) * mm, "radius": 3.18 * mm});
            skCircle(sketch, "E32.21.0", {"center": v(-15.94, 202.57) * mm, "radius": 3.18 * mm});
            skCircle(sketch, "E32.22.0", {"center": v(-31.79, 200.7) * mm, "radius": 3.18 * mm});
            skCircle(sketch, "E32.23.0", {"center": v(-47.44, 197.59) * mm, "radius": 3.18 * mm});
            skCircle(sketch, "E32.24.0", {"center": v(-62.8, 193.25) * mm, "radius": 3.18 * mm});
            skCircle(sketch, "E32.25.0", {"center": v(-77.76, 187.73) * mm, "radius": 3.18 * mm});
            skCircle(sketch, "E32.26.0", {"center": v(-92.25, 181.05) * mm, "radius": 3.18 * mm});
            skCircle(sketch, "E32.27.0", {"center": v(-106.17, 173.26) * mm, "radius": 3.18 * mm});
            skCircle(sketch, "E32.28.0", {"center": v(-119.44, 164.4) * mm, "radius": 3.17 * mm});
            skCircle(sketch, "E32.29.0", {"center": v(-131.97, 154.51) * mm, "radius": 3.18 * mm});
            skCircle(sketch, "E32.30.0", {"center": v(-143.68, 143.68) * mm, "radius": 3.18 * mm});
            skCircle(sketch, "E32.31.0", {"center": v(-154.51, 131.97) * mm, "radius": 3.18 * mm});
            skCircle(sketch, "E32.32.0", {"center": v(-164.4, 119.44) * mm, "radius": 3.18 * mm});
            skCircle(sketch, "E32.33.0", {"center": v(-173.26, 106.17) * mm, "radius": 3.18 * mm});
            skCircle(sketch, "E32.34.0", {"center": v(-181.05, 92.25) * mm, "radius": 3.18 * mm});
            skCircle(sketch, "E32.35.0", {"center": v(-187.73, 77.76) * mm, "radius": 3.18 * mm});
            skCircle(sketch, "E32.36.0", {"center": v(-193.25, 62.8) * mm, "radius": 3.18 * mm});
            skCircle(sketch, "E32.37.0", {"center": v(-197.59, 47.44) * mm, "radius": 3.18 * mm});
            skCircle(sketch, "E32.38.0", {"center": v(-200.7, 31.79) * mm, "radius": 3.18 * mm});
            skCircle(sketch, "E32.39.0", {"center": v(-202.57, 15.94) * mm, "radius": 3.18 * mm});
            skCircle(sketch, "E32.40.0", {"center": v(-203.2, 0) * mm, "radius": 3.18 * mm});
            skCircle(sketch, "E32.41.0", {"center": v(-202.57, -15.94) * mm, "radius": 3.18 * mm});
            skCircle(sketch, "E32.42.0", {"center": v(-200.7, -31.79) * mm, "radius": 3.18 * mm});
            skCircle(sketch, "E32.43.0", {"center": v(-197.59, -47.44) * mm, "radius": 3.18 * mm});
            skCircle(sketch, "E32.44.0", {"center": v(-193.25, -62.8) * mm, "radius": 3.18 * mm});
            skCircle(sketch, "E32.45.0", {"center": v(-187.73, -77.76) * mm, "radius": 3.18 * mm});
            skCircle(sketch, "E32.46.0", {"center": v(-181.05, -92.25) * mm, "radius": 3.18 * mm});
            skCircle(sketch, "E32.47.0", {"center": v(-173.26, -106.17) * mm, "radius": 3.18 * mm});
            skCircle(sketch, "E32.48.0", {"center": v(-164.4, -119.44) * mm, "radius": 3.18 * mm});
            skCircle(sketch, "E32.49.0", {"center": v(-154.51, -131.97) * mm, "radius": 3.18 * mm});
            skCircle(sketch, "E32.50.0", {"center": v(-143.68, -143.68) * mm, "radius": 3.18 * mm});
            skCircle(sketch, "E32.51.0", {"center": v(-131.97, -154.51) * mm, "radius": 3.18 * mm});
            skCircle(sketch, "E32.52.0", {"center": v(-119.44, -164.4) * mm, "radius": 3.18 * mm});
            skCircle(sketch, "E32.53.0", {"center": v(-106.17, -173.26) * mm, "radius": 3.18 * mm});
            skCircle(sketch, "E32.54.0", {"center": v(-92.25, -181.05) * mm, "radius": 3.18 * mm});
            skCircle(sketch, "E32.55.0", {"center": v(-77.76, -187.73) * mm, "radius": 3.18 * mm});
            skCircle(sketch, "E32.56.0", {"center": v(-62.8, -193.25) * mm, "radius": 3.18 * mm});
            skCircle(sketch, "E32.57.0", {"center": v(-47.44, -197.59) * mm, "radius": 3.18 * mm});
            skCircle(sketch, "E32.58.0", {"center": v(-31.79, -200.7) * mm, "radius": 3.17 * mm});
            skCircle(sketch, "E32.59.0", {"center": v(-15.94, -202.57) * mm, "radius": 3.18 * mm});
            skCircle(sketch, "E32.60.0", {"center": v(0, -203.2) * mm, "radius": 3.18 * mm});
            skCircle(sketch, "E32.61.0", {"center": v(15.94, -202.57) * mm, "radius": 3.18 * mm});
            skCircle(sketch, "E32.62.0", {"center": v(31.79, -200.7) * mm, "radius": 3.18 * mm});
            skCircle(sketch, "E32.63.0", {"center": v(47.44, -197.59) * mm, "radius": 3.18 * mm});
            skCircle(sketch, "E32.64.0", {"center": v(62.8, -193.25) * mm, "radius": 3.18 * mm});
            skCircle(sketch, "E32.65.0", {"center": v(77.76, -187.73) * mm, "radius": 3.18 * mm});
            skCircle(sketch, "E32.66.0", {"center": v(92.25, -181.05) * mm, "radius": 3.18 * mm});
            skCircle(sketch, "E32.67.0", {"center": v(106.17, -173.26) * mm, "radius": 3.18 * mm});
            skCircle(sketch, "E32.68.0", {"center": v(119.44, -164.4) * mm, "radius": 3.18 * mm});
            skCircle(sketch, "E32.69.0", {"center": v(131.97, -154.51) * mm, "radius": 3.18 * mm});
            skCircle(sketch, "E32.70.0", {"center": v(143.68, -143.68) * mm, "radius": 3.18 * mm});
            skCircle(sketch, "E32.71.0", {"center": v(154.51, -131.97) * mm, "radius": 3.18 * mm});
            skCircle(sketch, "E32.72.0", {"center": v(164.4, -119.44) * mm, "radius": 3.18 * mm});
            skCircle(sketch, "E32.73.0", {"center": v(173.26, -106.17) * mm, "radius": 3.18 * mm});
            skCircle(sketch, "E32.74.0", {"center": v(181.05, -92.25) * mm, "radius": 3.18 * mm});
            skCircle(sketch, "E32.75.0", {"center": v(187.73, -77.76) * mm, "radius": 3.18 * mm});
            skCircle(sketch, "E32.76.0", {"center": v(193.25, -62.8) * mm, "radius": 3.18 * mm});
            skCircle(sketch, "E32.77.0", {"center": v(197.59, -47.44) * mm, "radius": 3.18 * mm});
            skCircle(sketch, "E32.78.0", {"center": v(200.7, -31.79) * mm, "radius": 3.18 * mm});
            skCircle(sketch, "E32.79.0", {"center": v(202.57, -15.94) * mm, "radius": 3.18 * mm});
            skCircle(sketch, "E33.1.0", {"center": v(215.35, 15.4) * mm, "radius": 3.18 * mm});
            skCircle(sketch, "E33.2.0", {"center": v(213.7, 30.73) * mm, "radius": 3.18 * mm});
            skCircle(sketch, "E33.3.0", {"center": v(210.97, 45.9) * mm, "radius": 3.18 * mm});
            skCircle(sketch, "E33.4.0", {"center": v(207.15, 60.83) * mm, "radius": 3.18 * mm});
            skCircle(sketch, "E33.5.0", {"center": v(202.29, 75.45) * mm, "radius": 3.18 * mm});
            skCircle(sketch, "E33.6.0", {"center": v(196.39, 89.69) * mm, "radius": 3.18 * mm});
            skCircle(sketch, "E33.7.0", {"center": v(189.5, 103.47) * mm, "radius": 3.18 * mm});
            skCircle(sketch, "E33.8.0", {"center": v(181.63, 116.72) * mm, "radius": 3.18 * mm});
            skCircle(sketch, "E33.9.0", {"center": v(172.84, 129.38) * mm, "radius": 3.18 * mm});
            skCircle(sketch, "E33.10.0", {"center": v(163.17, 141.38) * mm, "radius": 3.18 * mm});
            skCircle(sketch, "E33.11.0", {"center": v(152.66, 152.66) * mm, "radius": 3.18 * mm});
            skCircle(sketch, "E33.12.0", {"center": v(141.38, 163.17) * mm, "radius": 3.18 * mm});
            skCircle(sketch, "E33.13.0", {"center": v(129.38, 172.84) * mm, "radius": 3.18 * mm});
            skCircle(sketch, "E33.14.0", {"center": v(116.72, 181.63) * mm, "radius": 3.18 * mm});
            skCircle(sketch, "E33.15.0", {"center": v(103.47, 189.5) * mm, "radius": 3.18 * mm});
            skCircle(sketch, "E33.16.0", {"center": v(89.69, 196.39) * mm, "radius": 3.18 * mm});
            skCircle(sketch, "E33.17.0", {"center": v(75.45, 202.29) * mm, "radius": 3.18 * mm});
            skCircle(sketch, "E33.18.0", {"center": v(60.83, 207.15) * mm, "radius": 3.18 * mm});
            skCircle(sketch, "E33.19.0", {"center": v(45.9, 210.97) * mm, "radius": 3.18 * mm});
            skCircle(sketch, "E33.20.0", {"center": v(30.73, 213.7) * mm, "radius": 3.18 * mm});
            skCircle(sketch, "E33.21.0", {"center": v(15.4, 215.35) * mm, "radius": 3.18 * mm});
            skCircle(sketch, "E33.22.0", {"center": v(0, 215.9) * mm, "radius": 3.18 * mm});
            skCircle(sketch, "E33.23.0", {"center": v(-15.4, 215.35) * mm, "radius": 3.18 * mm});
            skCircle(sketch, "E33.24.0", {"center": v(-30.73, 213.7) * mm, "radius": 3.18 * mm});
            skCircle(sketch, "E33.25.0", {"center": v(-45.9, 210.97) * mm, "radius": 3.18 * mm});
            skCircle(sketch, "E33.26.0", {"center": v(-60.83, 207.15) * mm, "radius": 3.18 * mm});
            skCircle(sketch, "E33.27.0", {"center": v(-75.45, 202.29) * mm, "radius": 3.18 * mm});
            skCircle(sketch, "E33.28.0", {"center": v(-89.69, 196.39) * mm, "radius": 3.18 * mm});
            skCircle(sketch, "E33.29.0", {"center": v(-103.47, 189.5) * mm, "radius": 3.18 * mm});
            skCircle(sketch, "E33.30.0", {"center": v(-116.72, 181.63) * mm, "radius": 3.18 * mm});
            skCircle(sketch, "E33.31.0", {"center": v(-129.38, 172.84) * mm, "radius": 3.18 * mm});
            skCircle(sketch, "E33.32.0", {"center": v(-141.38, 163.17) * mm, "radius": 3.18 * mm});
            skCircle(sketch, "E33.33.0", {"center": v(-152.66, 152.66) * mm, "radius": 3.18 * mm});
            skCircle(sketch, "E33.34.0", {"center": v(-163.17, 141.38) * mm, "radius": 3.18 * mm});
            skCircle(sketch, "E33.35.0", {"center": v(-172.84, 129.38) * mm, "radius": 3.18 * mm});
            skCircle(sketch, "E33.36.0", {"center": v(-181.63, 116.72) * mm, "radius": 3.18 * mm});
            skCircle(sketch, "E33.37.0", {"center": v(-189.5, 103.47) * mm, "radius": 3.18 * mm});
            skCircle(sketch, "E33.38.0", {"center": v(-196.39, 89.69) * mm, "radius": 3.18 * mm});
            skCircle(sketch, "E33.39.0", {"center": v(-202.29, 75.45) * mm, "radius": 3.18 * mm});
            skCircle(sketch, "E33.40.0", {"center": v(-207.15, 60.83) * mm, "radius": 3.18 * mm});
            skCircle(sketch, "E33.41.0", {"center": v(-210.97, 45.9) * mm, "radius": 3.18 * mm});
            skCircle(sketch, "E33.42.0", {"center": v(-213.7, 30.73) * mm, "radius": 3.18 * mm});
            skCircle(sketch, "E33.43.0", {"center": v(-215.35, 15.4) * mm, "radius": 3.18 * mm});
            skCircle(sketch, "E33.44.0", {"center": v(-215.9, 0) * mm, "radius": 3.18 * mm});
            skCircle(sketch, "E33.45.0", {"center": v(-215.35, -15.4) * mm, "radius": 3.18 * mm});
            skCircle(sketch, "E33.46.0", {"center": v(-213.7, -30.73) * mm, "radius": 3.18 * mm});
            skCircle(sketch, "E33.47.0", {"center": v(-210.97, -45.9) * mm, "radius": 3.18 * mm});
            skCircle(sketch, "E33.48.0", {"center": v(-207.15, -60.83) * mm, "radius": 3.18 * mm});
            skCircle(sketch, "E33.49.0", {"center": v(-202.29, -75.45) * mm, "radius": 3.18 * mm});
            skCircle(sketch, "E33.50.0", {"center": v(-196.39, -89.69) * mm, "radius": 3.18 * mm});
            skCircle(sketch, "E33.51.0", {"center": v(-189.5, -103.47) * mm, "radius": 3.18 * mm});
            skCircle(sketch, "E33.52.0", {"center": v(-181.63, -116.72) * mm, "radius": 3.18 * mm});
            skCircle(sketch, "E33.53.0", {"center": v(-172.84, -129.38) * mm, "radius": 3.18 * mm});
            skCircle(sketch, "E33.54.0", {"center": v(-163.17, -141.38) * mm, "radius": 3.18 * mm});
            skCircle(sketch, "E33.55.0", {"center": v(-152.66, -152.66) * mm, "radius": 3.18 * mm});
            skCircle(sketch, "E33.56.0", {"center": v(-141.38, -163.17) * mm, "radius": 3.18 * mm});
            skCircle(sketch, "E33.57.0", {"center": v(-129.38, -172.84) * mm, "radius": 3.18 * mm});
            skCircle(sketch, "E33.58.0", {"center": v(-116.72, -181.63) * mm, "radius": 3.18 * mm});
            skCircle(sketch, "E33.59.0", {"center": v(-103.47, -189.5) * mm, "radius": 3.18 * mm});
            skCircle(sketch, "E33.60.0", {"center": v(-89.69, -196.39) * mm, "radius": 3.18 * mm});
            skCircle(sketch, "E33.61.0", {"center": v(-75.45, -202.29) * mm, "radius": 3.18 * mm});
            skCircle(sketch, "E33.62.0", {"center": v(-60.83, -207.15) * mm, "radius": 3.18 * mm});
            skCircle(sketch, "E33.63.0", {"center": v(-45.9, -210.97) * mm, "radius": 3.18 * mm});
            skCircle(sketch, "E33.64.0", {"center": v(-30.73, -213.7) * mm, "radius": 3.18 * mm});
            skCircle(sketch, "E33.65.0", {"center": v(-15.4, -215.35) * mm, "radius": 3.18 * mm});
            skCircle(sketch, "E33.66.0", {"center": v(0, -215.9) * mm, "radius": 3.18 * mm});
            skCircle(sketch, "E33.67.0", {"center": v(15.4, -215.35) * mm, "radius": 3.18 * mm});
            skCircle(sketch, "E33.68.0", {"center": v(30.73, -213.7) * mm, "radius": 3.18 * mm});
            skCircle(sketch, "E33.69.0", {"center": v(45.9, -210.97) * mm, "radius": 3.18 * mm});
            skCircle(sketch, "E33.70.0", {"center": v(60.83, -207.15) * mm, "radius": 3.18 * mm});
            skCircle(sketch, "E33.71.0", {"center": v(75.45, -202.29) * mm, "radius": 3.18 * mm});
            skCircle(sketch, "E33.72.0", {"center": v(89.69, -196.39) * mm, "radius": 3.18 * mm});
            skCircle(sketch, "E33.73.0", {"center": v(103.47, -189.5) * mm, "radius": 3.18 * mm});
            skCircle(sketch, "E33.74.0", {"center": v(116.72, -181.63) * mm, "radius": 3.18 * mm});
            skCircle(sketch, "E33.75.0", {"center": v(129.38, -172.84) * mm, "radius": 3.18 * mm});
            skCircle(sketch, "E33.76.0", {"center": v(141.38, -163.17) * mm, "radius": 3.18 * mm});
            skCircle(sketch, "E33.77.0", {"center": v(152.66, -152.66) * mm, "radius": 3.18 * mm});
            skCircle(sketch, "E33.78.0", {"center": v(163.17, -141.38) * mm, "radius": 3.18 * mm});
            skCircle(sketch, "E33.79.0", {"center": v(172.84, -129.38) * mm, "radius": 3.18 * mm});
            skCircle(sketch, "E33.80.0", {"center": v(181.63, -116.72) * mm, "radius": 3.18 * mm});
            skCircle(sketch, "E33.81.0", {"center": v(189.5, -103.47) * mm, "radius": 3.18 * mm});
            skCircle(sketch, "E33.82.0", {"center": v(196.39, -89.69) * mm, "radius": 3.18 * mm});
            skCircle(sketch, "E33.83.0", {"center": v(202.29, -75.45) * mm, "radius": 3.18 * mm});
            skCircle(sketch, "E33.84.0", {"center": v(207.15, -60.83) * mm, "radius": 3.18 * mm});
            skCircle(sketch, "E33.85.0", {"center": v(210.97, -45.9) * mm, "radius": 3.18 * mm});
            skCircle(sketch, "E33.86.0", {"center": v(213.7, -30.73) * mm, "radius": 3.18 * mm});
            skCircle(sketch, "E33.87.0", {"center": v(215.35, -15.4) * mm, "radius": 3.18 * mm});
            skCircle(sketch, "E34.1.0", {"center": v(228.04, 15.95) * mm, "radius": 3.18 * mm});
            skCircle(sketch, "E34.2.0", {"center": v(226.38, 31.81) * mm, "radius": 3.18 * mm});
            skCircle(sketch, "E34.3.0", {"center": v(223.6, 47.53) * mm, "radius": 3.18 * mm});
            skCircle(sketch, "E34.4.0", {"center": v(219.74, 63.01) * mm, "radius": 3.18 * mm});
            skCircle(sketch, "E34.5.0", {"center": v(214.81, 78.19) * mm, "radius": 3.18 * mm});
            skCircle(sketch, "E34.6.0", {"center": v(208.84, 92.98) * mm, "radius": 3.18 * mm});
            skCircle(sketch, "E34.7.0", {"center": v(201.84, 107.32) * mm, "radius": 3.18 * mm});
            skCircle(sketch, "E34.8.0", {"center": v(193.86, 121.14) * mm, "radius": 3.18 * mm});
            skCircle(sketch, "E34.9.0", {"center": v(184.94, 134.37) * mm, "radius": 3.18 * mm});
            skCircle(sketch, "E34.10.0", {"center": v(175.12, 146.94) * mm, "radius": 3.18 * mm});
            skCircle(sketch, "E34.11.0", {"center": v(164.44, 158.8) * mm, "radius": 3.18 * mm});
            skCircle(sketch, "E34.12.0", {"center": v(152.96, 169.88) * mm, "radius": 3.17 * mm});
            skCircle(sketch, "E34.13.0", {"center": v(140.74, 180.14) * mm, "radius": 3.18 * mm});
            skCircle(sketch, "E34.14.0", {"center": v(127.83, 189.52) * mm, "radius": 3.18 * mm});
            skCircle(sketch, "E34.15.0", {"center": v(114.3, 197.97) * mm, "radius": 3.18 * mm});
            skCircle(sketch, "E34.16.0", {"center": v(100.21, 205.46) * mm, "radius": 3.18 * mm});
            skCircle(sketch, "E34.17.0", {"center": v(85.64, 211.95) * mm, "radius": 3.18 * mm});
            skCircle(sketch, "E34.18.0", {"center": v(70.64, 217.41) * mm, "radius": 3.18 * mm});
            skCircle(sketch, "E34.19.0", {"center": v(55.3, 221.8) * mm, "radius": 3.18 * mm});
            skCircle(sketch, "E34.20.0", {"center": v(39.7, 225.13) * mm, "radius": 3.18 * mm});
            skCircle(sketch, "E34.21.0", {"center": v(23.9, 227.35) * mm, "radius": 3.18 * mm});
            skCircle(sketch, "E34.22.0", {"center": v(7.98, 228.46) * mm, "radius": 3.18 * mm});
            skCircle(sketch, "E34.23.0", {"center": v(-7.98, 228.46) * mm, "radius": 3.18 * mm});
            skCircle(sketch, "E34.24.0", {"center": v(-23.9, 227.35) * mm, "radius": 3.18 * mm});
            skCircle(sketch, "E34.25.0", {"center": v(-39.7, 225.13) * mm, "radius": 3.18 * mm});
            skCircle(sketch, "E34.26.0", {"center": v(-55.3, 221.8) * mm, "radius": 3.18 * mm});
            skCircle(sketch, "E34.27.0", {"center": v(-70.64, 217.41) * mm, "radius": 3.18 * mm});
            skCircle(sketch, "E34.28.0", {"center": v(-85.64, 211.95) * mm, "radius": 3.18 * mm});
            skCircle(sketch, "E34.29.0", {"center": v(-100.21, 205.46) * mm, "radius": 3.17 * mm});
            skCircle(sketch, "E34.30.0", {"center": v(-114.3, 197.97) * mm, "radius": 3.18 * mm});
            skCircle(sketch, "E34.31.0", {"center": v(-127.83, 189.52) * mm, "radius": 3.17 * mm});
            skCircle(sketch, "E34.32.0", {"center": v(-140.74, 180.14) * mm, "radius": 3.18 * mm});
            skCircle(sketch, "E34.33.0", {"center": v(-152.96, 169.88) * mm, "radius": 3.18 * mm});
            skCircle(sketch, "E34.34.0", {"center": v(-164.44, 158.8) * mm, "radius": 3.17 * mm});
            skCircle(sketch, "E34.35.0", {"center": v(-175.12, 146.94) * mm, "radius": 3.18 * mm});
            skCircle(sketch, "E34.36.0", {"center": v(-184.94, 134.37) * mm, "radius": 3.18 * mm});
            skCircle(sketch, "E34.37.0", {"center": v(-193.86, 121.14) * mm, "radius": 3.18 * mm});
            skCircle(sketch, "E34.38.0", {"center": v(-201.84, 107.32) * mm, "radius": 3.18 * mm});
            skCircle(sketch, "E34.39.0", {"center": v(-208.84, 92.98) * mm, "radius": 3.18 * mm});
            skCircle(sketch, "E34.40.0", {"center": v(-214.81, 78.19) * mm, "radius": 3.18 * mm});
            skCircle(sketch, "E34.41.0", {"center": v(-219.74, 63.01) * mm, "radius": 3.18 * mm});
            skCircle(sketch, "E34.42.0", {"center": v(-223.6, 47.53) * mm, "radius": 3.18 * mm});
            skCircle(sketch, "E34.43.0", {"center": v(-226.38, 31.81) * mm, "radius": 3.18 * mm});
            skCircle(sketch, "E34.44.0", {"center": v(-228.04, 15.95) * mm, "radius": 3.18 * mm});
            skCircle(sketch, "E34.45.0", {"center": v(-228.6, 0) * mm, "radius": 3.18 * mm});
            skCircle(sketch, "E34.46.0", {"center": v(-228.04, -15.95) * mm, "radius": 3.18 * mm});
            skCircle(sketch, "E34.47.0", {"center": v(-226.38, -31.81) * mm, "radius": 3.17 * mm});
            skCircle(sketch, "E34.48.0", {"center": v(-223.6, -47.53) * mm, "radius": 3.18 * mm});
            skCircle(sketch, "E34.49.0", {"center": v(-219.74, -63.01) * mm, "radius": 3.18 * mm});
            skCircle(sketch, "E34.50.0", {"center": v(-214.81, -78.19) * mm, "radius": 3.18 * mm});
            skCircle(sketch, "E34.51.0", {"center": v(-208.84, -92.98) * mm, "radius": 3.18 * mm});
            skCircle(sketch, "E34.52.0", {"center": v(-201.84, -107.32) * mm, "radius": 3.18 * mm});
            skCircle(sketch, "E34.53.0", {"center": v(-193.86, -121.14) * mm, "radius": 3.18 * mm});
            skCircle(sketch, "E34.54.0", {"center": v(-184.94, -134.37) * mm, "radius": 3.18 * mm});
            skCircle(sketch, "E34.55.0", {"center": v(-175.12, -146.94) * mm, "radius": 3.17 * mm});
            skCircle(sketch, "E34.56.0", {"center": v(-164.44, -158.8) * mm, "radius": 3.18 * mm});
            skCircle(sketch, "E34.57.0", {"center": v(-152.96, -169.88) * mm, "radius": 3.18 * mm});
            skCircle(sketch, "E34.58.0", {"center": v(-140.74, -180.14) * mm, "radius": 3.18 * mm});
            skCircle(sketch, "E34.59.0", {"center": v(-127.83, -189.52) * mm, "radius": 3.18 * mm});
            skCircle(sketch, "E34.60.0", {"center": v(-114.3, -197.97) * mm, "radius": 3.18 * mm});
            skCircle(sketch, "E34.61.0", {"center": v(-100.21, -205.46) * mm, "radius": 3.18 * mm});
            skCircle(sketch, "E34.62.0", {"center": v(-85.64, -211.95) * mm, "radius": 3.18 * mm});
            skCircle(sketch, "E34.63.0", {"center": v(-70.64, -217.41) * mm, "radius": 3.18 * mm});
            skCircle(sketch, "E34.64.0", {"center": v(-55.3, -221.8) * mm, "radius": 3.18 * mm});
            skCircle(sketch, "E34.65.0", {"center": v(-39.7, -225.13) * mm, "radius": 3.18 * mm});
            skCircle(sketch, "E34.66.0", {"center": v(-23.9, -227.35) * mm, "radius": 3.18 * mm});
            skCircle(sketch, "E34.67.0", {"center": v(-7.98, -228.46) * mm, "radius": 3.17 * mm});
            skCircle(sketch, "E34.68.0", {"center": v(7.98, -228.46) * mm, "radius": 3.18 * mm});
            skCircle(sketch, "E34.69.0", {"center": v(23.9, -227.35) * mm, "radius": 3.18 * mm});
            skCircle(sketch, "E34.70.0", {"center": v(39.7, -225.13) * mm, "radius": 3.18 * mm});
            skCircle(sketch, "E34.71.0", {"center": v(55.3, -221.8) * mm, "radius": 3.18 * mm});
            skCircle(sketch, "E34.72.0", {"center": v(70.64, -217.41) * mm, "radius": 3.18 * mm});
            skCircle(sketch, "E34.73.0", {"center": v(85.64, -211.95) * mm, "radius": 3.18 * mm});
            skCircle(sketch, "E34.74.0", {"center": v(100.21, -205.46) * mm, "radius": 3.18 * mm});
            skCircle(sketch, "E34.75.0", {"center": v(114.3, -197.97) * mm, "radius": 3.18 * mm});
            skCircle(sketch, "E34.76.0", {"center": v(127.83, -189.52) * mm, "radius": 3.18 * mm});
            skCircle(sketch, "E34.77.0", {"center": v(140.74, -180.14) * mm, "radius": 3.18 * mm});
            skCircle(sketch, "E34.78.0", {"center": v(152.96, -169.88) * mm, "radius": 3.18 * mm});
            skCircle(sketch, "E34.79.0", {"center": v(164.44, -158.8) * mm, "radius": 3.18 * mm});
            skCircle(sketch, "E34.80.0", {"center": v(175.12, -146.94) * mm, "radius": 3.18 * mm});
            skCircle(sketch, "E34.81.0", {"center": v(184.94, -134.37) * mm, "radius": 3.18 * mm});
            skCircle(sketch, "E34.82.0", {"center": v(193.86, -121.14) * mm, "radius": 3.18 * mm});
            skCircle(sketch, "E34.83.0", {"center": v(201.84, -107.32) * mm, "radius": 3.18 * mm});
            skCircle(sketch, "E34.84.0", {"center": v(208.84, -92.98) * mm, "radius": 3.18 * mm});
            skCircle(sketch, "E34.85.0", {"center": v(214.81, -78.19) * mm, "radius": 3.18 * mm});
            skCircle(sketch, "E34.86.0", {"center": v(219.74, -63.01) * mm, "radius": 3.18 * mm});
            skCircle(sketch, "E34.87.0", {"center": v(223.6, -47.53) * mm, "radius": 3.18 * mm});
            skCircle(sketch, "E34.88.0", {"center": v(226.38, -31.81) * mm, "radius": 3.18 * mm});
            skCircle(sketch, "E34.89.0", {"center": v(228.04, -15.95) * mm, "radius": 3.18 * mm});
            skSolve(sketch);
        }
        {
            var Q0;
            {var subQ1=sQuery(id+"F0.wireOp",EDGE,"E0.top");var subQ6=sQuery(id+"F0.wireOp",EDGE,"E0.left");var subQ9=makeQuery(id+"F0.imprint","INTERSECT",VERTEX,{"derivedFrom":[subQ1,subQ6]});Q0=makeQuery(id+"F0.imprint","IMPRINT",FACE,{"disambiguationData":[TD([[makeQuery(id+"F0.imprint","IMPRINT",EDGE,{"disambiguationData":[TD([[subQ9,-1.0]])],"derivedFrom":subQ1}),1.0]])]});}
            var Q1;
            {var subQ5=sQuery(id+"F0.wireOp",EDGE,"E0.top");var subQ7=sQuery(id+"F0.wireOp",EDGE,"JAwSw2JL-n3NN-2Vln-OLVn-L8GvoOgm2xYq");var subQ8=makeQuery(id+"F0.imprint","INTERSECT",VERTEX,{"derivedFrom":[subQ5,subQ7]});Q1=makeQuery(id+"F0.imprint","IMPRINT",FACE,{"disambiguationData":[TD([[makeQuery(id+"F0.imprint","IMPRINT",EDGE,{"disambiguationData":[TD([[subQ8,-1.0]])],"derivedFrom":subQ5}),1.0]])]});}
            var Q2;
            {var subQ1=sQuery(id+"F0.wireOp",EDGE,"e8252f44-7828-416d-82ac-373ce15db359");var subQ5=sQuery(id+"F0.wireOp",EDGE,"23pqLXLV-SrZZ-kslz-O0l0-19fHHKHyzlwI");var subQ6=makeQuery(id+"F0.imprint","INTERSECT",VERTEX,{"disambiguationData":[OD(1.0)],"derivedFrom":[subQ1,subQ5]});Q2=makeQuery(id+"F0.imprint","IMPRINT",FACE,{"disambiguationData":[TD([[makeQuery(id+"F0.imprint","IMPRINT",EDGE,{"disambiguationData":[TD([[subQ6,-1.0]])],"derivedFrom":subQ1}),-1.0]])]});}
            var Q3;
            {var subQ1=sQuery(id+"F0.wireOp",EDGE,"E0.left");var subQ5=sQuery(id+"F0.wireOp",EDGE,"23pqLXLV-SrZZ-kslz-O0l0-19fHHKHyzlwI");var subQ6=makeQuery(id+"F0.imprint","INTERSECT",VERTEX,{"derivedFrom":[subQ1,subQ5]});Q3=makeQuery(id+"F0.imprint","IMPRINT",FACE,{"disambiguationData":[TD([[makeQuery(id+"F0.imprint","IMPRINT",EDGE,{"disambiguationData":[TD([[subQ6,-1.0]])],"derivedFrom":subQ1}),1.0]])]});}
            var Q4;
            {var subQ1=sQuery(id+"F0.wireOp",EDGE,"E0.left");var subQ5=sQuery(id+"F0.wireOp",EDGE,"ks5EaK8h-8Zo1-6vaX-m6YF-OaYFmNDyZiSu");var subQ6=makeQuery(id+"F0.imprint","INTERSECT",VERTEX,{"derivedFrom":[subQ1,subQ5]});Q4=makeQuery(id+"F0.imprint","IMPRINT",FACE,{"disambiguationData":[TD([[makeQuery(id+"F0.imprint","IMPRINT",EDGE,{"disambiguationData":[TD([[subQ6,-1.0]])],"derivedFrom":subQ1}),1.0]])]});}
            var Q5;
            {var subQ0=sQuery(id+"F0.wireOp",EDGE,"OUGwM7Ne-J0Vz-JpQP-Of8x-XZFFkOnO35nF");var subQ1=sQuery(id+"F0.wireOp",EDGE,"e8252f44-7828-416d-82ac-373ce15db359");var subQ2=makeQuery(id+"F0.imprint","INTERSECT",VERTEX,{"disambiguationData":[OD(0.0)],"derivedFrom":[subQ1,subQ0]});Q5=makeQuery(id+"F0.imprint","IMPRINT",FACE,{"disambiguationData":[TD([[makeQuery(id+"F0.imprint","IMPRINT",EDGE,{"disambiguationData":[TD([[subQ2,-1.0]])],"derivedFrom":subQ1}),-1.0]])]});}
            var Q6;
            {var subQ1=sQuery(id+"F0.wireOp",EDGE,"E0.bottom");var subQ5=sQuery(id+"F0.wireOp",EDGE,"JAwSw2JL-n3NN-2Vln-OLVn-L8GvoOgm2xYq");var subQ6=makeQuery(id+"F0.imprint","INTERSECT",VERTEX,{"derivedFrom":[subQ1,subQ5]});Q6=makeQuery(id+"F0.imprint","IMPRINT",FACE,{"disambiguationData":[TD([[makeQuery(id+"F0.imprint","IMPRINT",EDGE,{"disambiguationData":[TD([[subQ6,-1.0]])],"derivedFrom":subQ1}),-1.0]])]});}
            var Q7;
            {var subQ1=sQuery(id+"F0.wireOp",EDGE,"E0.left");var subQ5=sQuery(id+"F0.wireOp",EDGE,"E0.bottom");var subQ6=makeQuery(id+"F0.imprint","INTERSECT",VERTEX,{"derivedFrom":[subQ5,subQ1]});Q7=makeQuery(id+"F0.imprint","IMPRINT",FACE,{"disambiguationData":[TD([[makeQuery(id+"F0.imprint","IMPRINT",EDGE,{"disambiguationData":[TD([[subQ6,-1.0]])],"derivedFrom":subQ5}),-1.0]])]});}
            var Q8;
            {var subQ1=sQuery(id+"F0.wireOp",EDGE,"E0.right");var subQ6=sQuery(id+"F0.wireOp",EDGE,"E0.bottom");var subQ9=makeQuery(id+"F0.imprint","INTERSECT",VERTEX,{"derivedFrom":[subQ6,subQ1]});Q8=makeQuery(id+"F0.imprint","IMPRINT",FACE,{"disambiguationData":[TD([[makeQuery(id+"F0.imprint","IMPRINT",EDGE,{"disambiguationData":[TD([[subQ9,1.0]])],"derivedFrom":subQ6}),-1.0]])]});}
            var Q9;
            {var subQ1=sQuery(id+"F0.wireOp",EDGE,"E0.bottom");var subQ5=sQuery(id+"F0.wireOp",EDGE,"OUGwM7Ne-J0Vz-JpQP-Of8x-XZFFkOnO35nF");var subQ6=makeQuery(id+"F0.imprint","INTERSECT",VERTEX,{"derivedFrom":[subQ1,subQ5]});Q9=makeQuery(id+"F0.imprint","IMPRINT",FACE,{"disambiguationData":[TD([[makeQuery(id+"F0.imprint","IMPRINT",EDGE,{"disambiguationData":[TD([[subQ6,-1.0]])],"derivedFrom":subQ1}),-1.0]])]});}
            var Q10;
            {var subQ7=sQuery(id+"F0.wireOp",EDGE,"OUGwM7Ne-J0Vz-JpQP-Of8x-XZFFkOnO35nF");var subQ8=sQuery(id+"F0.wireOp",EDGE,"e8252f44-7828-416d-82ac-373ce15db359");var subQ9=makeQuery(id+"F0.imprint","INTERSECT",VERTEX,{"disambiguationData":[OD(0.0)],"derivedFrom":[subQ8,subQ7]});Q10=makeQuery(id+"F0.imprint","IMPRINT",FACE,{"disambiguationData":[TD([[makeQuery(id+"F0.imprint","IMPRINT",EDGE,{"disambiguationData":[TD([[subQ9,1.0]])],"derivedFrom":subQ8}),-1.0]])]});}
            var Q11;
            {var subQ0=sQuery(id+"F0.wireOp",EDGE,"ks5EaK8h-8Zo1-6vaX-m6YF-OaYFmNDyZiSu");var subQ1=sQuery(id+"F0.wireOp",EDGE,"E0.right");var subQ2=makeQuery(id+"F0.imprint","INTERSECT",VERTEX,{"derivedFrom":[subQ1,subQ0]});Q11=makeQuery(id+"F0.imprint","IMPRINT",FACE,{"disambiguationData":[TD([[makeQuery(id+"F0.imprint","IMPRINT",EDGE,{"disambiguationData":[TD([[subQ2,-1.0]])],"derivedFrom":subQ1}),-1.0]])]});}
            var Q12;
            {var subQ0=sQuery(id+"F0.wireOp",EDGE,"23pqLXLV-SrZZ-kslz-O0l0-19fHHKHyzlwI");var subQ1=sQuery(id+"F0.wireOp",EDGE,"e8252f44-7828-416d-82ac-373ce15db359");var subQ2=makeQuery(id+"F0.imprint","INTERSECT",VERTEX,{"disambiguationData":[OD(0.0)],"derivedFrom":[subQ1,subQ0]});Q12=makeQuery(id+"F0.imprint","IMPRINT",FACE,{"disambiguationData":[TD([[makeQuery(id+"F0.imprint","IMPRINT",EDGE,{"disambiguationData":[TD([[subQ2,1.0]])],"derivedFrom":subQ1}),-1.0]])]});}
            var Q13;
            {var subQ0=sQuery(id+"F0.wireOp",EDGE,"23pqLXLV-SrZZ-kslz-O0l0-19fHHKHyzlwI");var subQ1=sQuery(id+"F0.wireOp",EDGE,"E0.right");var subQ2=makeQuery(id+"F0.imprint","INTERSECT",VERTEX,{"derivedFrom":[subQ1,subQ0]});Q13=makeQuery(id+"F0.imprint","IMPRINT",FACE,{"disambiguationData":[TD([[makeQuery(id+"F0.imprint","IMPRINT",EDGE,{"disambiguationData":[TD([[subQ2,-1.0]])],"derivedFrom":subQ1}),-1.0]])]});}
            var Q14;
            {var subQ1=sQuery(id+"F0.wireOp",EDGE,"OUGwM7Ne-J0Vz-JpQP-Of8x-XZFFkOnO35nF");var subQ5=sQuery(id+"F0.wireOp",EDGE,"E0.top");var subQ6=makeQuery(id+"F0.imprint","INTERSECT",VERTEX,{"derivedFrom":[subQ5,subQ1]});Q14=makeQuery(id+"F0.imprint","IMPRINT",FACE,{"disambiguationData":[TD([[makeQuery(id+"F0.imprint","IMPRINT",EDGE,{"disambiguationData":[TD([[subQ6,-1.0]])],"derivedFrom":subQ5}),1.0]])]});}
            var Q15;
            {var subQ1=sQuery(id+"F0.wireOp",EDGE,"E0.right");var subQ6=sQuery(id+"F0.wireOp",EDGE,"E0.top");var subQ9=makeQuery(id+"F0.imprint","INTERSECT",VERTEX,{"derivedFrom":[subQ6,subQ1]});Q15=makeQuery(id+"F0.imprint","IMPRINT",FACE,{"disambiguationData":[TD([[makeQuery(id+"F0.imprint","IMPRINT",EDGE,{"disambiguationData":[TD([[subQ9,1.0]])],"derivedFrom":subQ6}),1.0]])]});}
            extrude(context, id + "F1", {"entities" : qUnion([Q0, Q1, Q2, Q3, Q4, Q5, Q6, Q7, Q8, Q9, Q10, Q11, Q12, Q13, Q14, Q15]), "depth" : 3.8 * mm});
        }
    });
